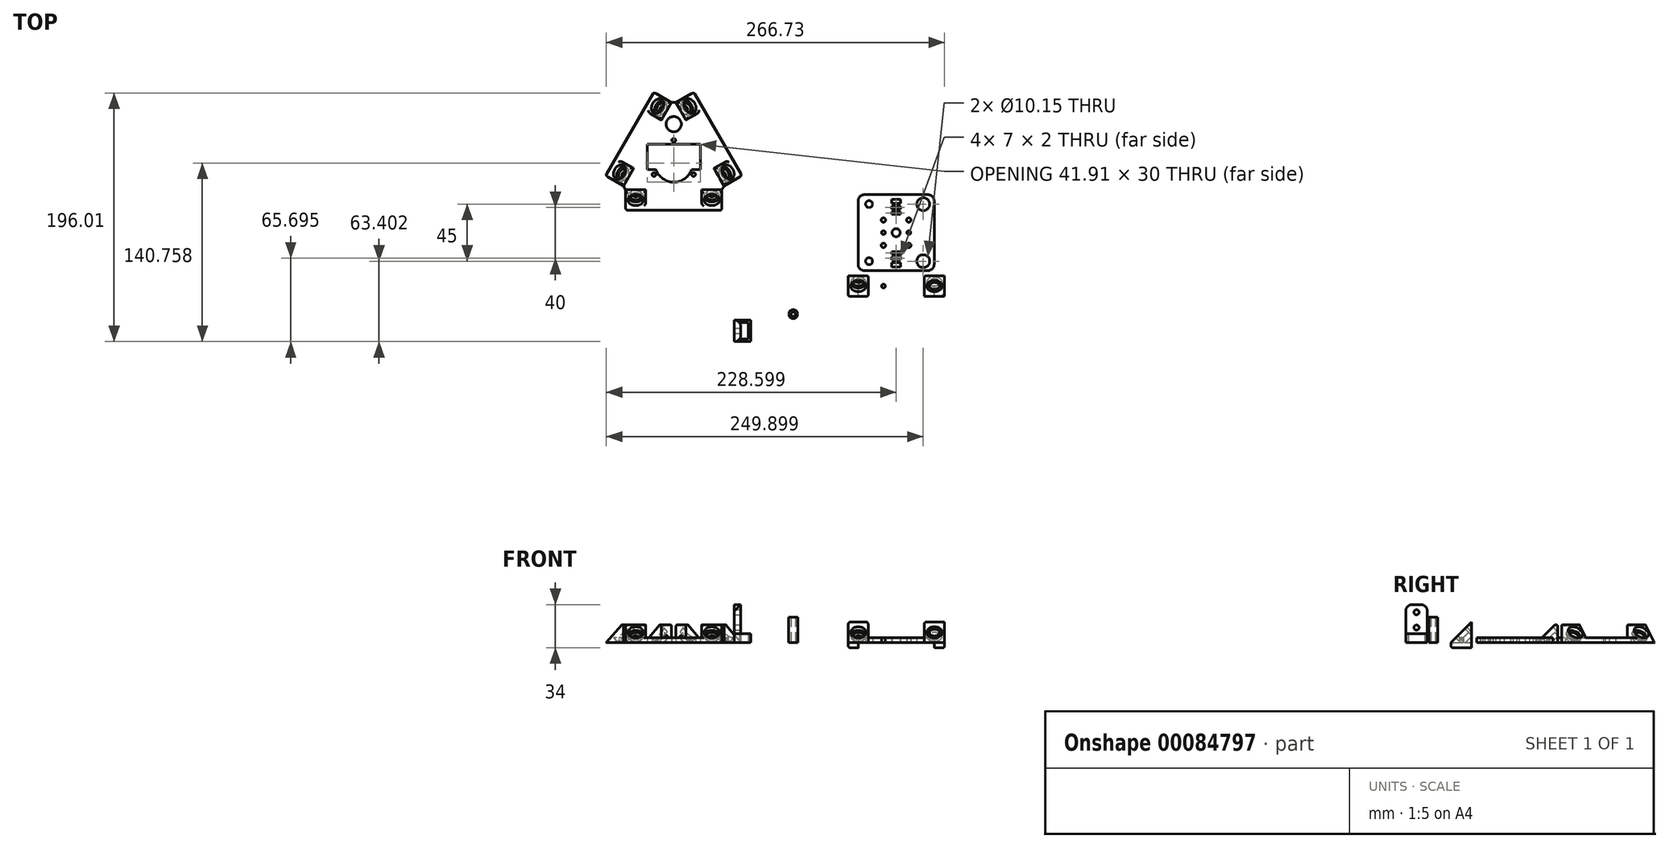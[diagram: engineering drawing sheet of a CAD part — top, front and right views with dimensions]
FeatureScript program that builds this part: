
annotation { "Feature Type Name" : "Feature", "Feature Type Description" : "" }
export const myFeature = defineFeature(function(context is Context, id is Id, definition is map)
    precondition{}
    {
        {
            var Q0;
            Q0=qCreatedBy(makeId("Top.planeOp"),FACE);
            var sketch = newSketch(context, id + "F0", { "sketchPlane" : qUnion([Q0])});
            skArc(sketch, "E0", {"start": v(24.79, -19.87) * mm, "mid": v(28.33, -18.4) * mm, "end": v(29.79, -14.87) * mm});
            skLineSegment(sketch, "E1", {"start": v(24.79, -19.87) * mm, "end": v(-25.21, -19.87) * mm});
            skArc(sketch, "E2", {"start": v(29.79, 35.13) * mm, "mid": v(28.33, 38.67) * mm, "end": v(24.79, 40.13) * mm});
            skLineSegment(sketch, "E3", {"start": v(29.79, 35.13) * mm, "end": v(29.79, -14.87) * mm});
            skArc(sketch, "E4", {"start": v(-25.21, 40.13) * mm, "mid": v(-28.75, 38.67) * mm, "end": v(-30.21, 35.13) * mm});
            skLineSegment(sketch, "E5", {"start": v(-25.21, 40.13) * mm, "end": v(24.79, 40.13) * mm});
            skArc(sketch, "E6", {"start": v(-30.21, -14.87) * mm, "mid": v(-28.75, -18.4) * mm, "end": v(-25.21, -19.87) * mm});
            skLineSegment(sketch, "E7", {"start": v(-30.21, -14.87) * mm, "end": v(-30.21, 35.13) * mm});
            skCircle(sketch, "E8", {"center": v(30, -32.16) * mm, "radius": 5.9 * mm, "construction": true});
            skCircle(sketch, "E9", {"center": v(-30, -32.16) * mm, "radius": 5.9 * mm, "construction": true});
            skLineSegment(sketch, "E10", {"start": v(-30.85, -40.13) * mm, "end": v(30.85, -40.13) * mm});
            skLineSegment(sketch, "E11", {"start": v(30.85, -23.83) * mm, "end": v(-30.85, -23.83) * mm});
            skCircle(sketch, "E12", {"center": v(21.14, 32.63) * mm, "radius": 5.08 * mm});
            skCircle(sketch, "E13", {"center": v(21.14, -12.37) * mm, "radius": 5.08 * mm});
            skCircle(sketch, "E14", {"center": v(-21.56, 32.63) * mm, "radius": 2.75 * mm});
            skCircle(sketch, "E15", {"center": v(-21.56, -12.37) * mm, "radius": 2.75 * mm});
            skCircle(sketch, "E16", {"center": v(-10.21, 20.13) * mm, "radius": 1.75 * mm});
            skCircle(sketch, "E17", {"center": v(-10.21, 0.13) * mm, "radius": 1.75 * mm});
            skCircle(sketch, "E18", {"center": v(9.79, 0.13) * mm, "radius": 1.75 * mm});
            skCircle(sketch, "E19", {"center": v(9.79, 20.13) * mm, "radius": 1.75 * mm});
            skLineSegment(sketch, "E20", {"start": v(-3.63, -6.88) * mm, "end": v(3.37, -6.88) * mm});
            skLineSegment(sketch, "E21", {"start": v(3.37, -6.88) * mm, "end": v(3.37, -4.88) * mm});
            skLineSegment(sketch, "E22", {"start": v(3.37, -4.88) * mm, "end": v(-3.63, -4.88) * mm});
            skLineSegment(sketch, "E23", {"start": v(-3.63, -4.88) * mm, "end": v(-3.63, -6.88) * mm});
            skLineSegment(sketch, "E24", {"start": v(-3.66, -11.08) * mm, "end": v(3.34, -11.08) * mm});
            skLineSegment(sketch, "E25", {"start": v(3.34, -11.08) * mm, "end": v(3.34, -9.08) * mm});
            skLineSegment(sketch, "E26", {"start": v(3.34, -9.08) * mm, "end": v(-3.66, -9.08) * mm});
            skLineSegment(sketch, "E27", {"start": v(-3.66, -9.08) * mm, "end": v(-3.66, -11.08) * mm});
            skLineSegment(sketch, "E28", {"start": v(3.35, -16.82) * mm, "end": v(3.35, -13.38) * mm});
            skLineSegment(sketch, "E29", {"start": v(3.35, -13.38) * mm, "end": v(-3.63, -13.38) * mm});
            skLineSegment(sketch, "E30", {"start": v(-3.63, 33.12) * mm, "end": v(3.37, 33.12) * mm});
            skLineSegment(sketch, "E31", {"start": v(3.37, 33.12) * mm, "end": v(3.37, 36.53) * mm});
            skLineSegment(sketch, "E32", {"start": v(3.37, 36.53) * mm, "end": v(-3.63, 36.52) * mm});
            skLineSegment(sketch, "E33", {"start": v(-3.63, 36.52) * mm, "end": v(-3.63, 33.12) * mm});
            skLineSegment(sketch, "E34", {"start": v(-3.66, 28.92) * mm, "end": v(3.34, 28.92) * mm});
            skLineSegment(sketch, "E35", {"start": v(3.34, 28.92) * mm, "end": v(3.34, 30.92) * mm});
            skLineSegment(sketch, "E36", {"start": v(3.34, 30.92) * mm, "end": v(-3.66, 30.92) * mm});
            skLineSegment(sketch, "E37", {"start": v(-3.66, 30.92) * mm, "end": v(-3.66, 28.92) * mm});
            skLineSegment(sketch, "E38", {"start": v(-3.63, 24.62) * mm, "end": v(3.37, 24.62) * mm});
            skLineSegment(sketch, "E39", {"start": v(3.37, 24.62) * mm, "end": v(3.37, 26.62) * mm});
            skLineSegment(sketch, "E40", {"start": v(3.37, 26.62) * mm, "end": v(-3.63, 26.62) * mm});
            skLineSegment(sketch, "E41", {"start": v(-3.63, 26.62) * mm, "end": v(-3.63, 24.62) * mm});
            skCircle(sketch, "E42", {"center": v(-10.21, 10.13) * mm, "radius": 1.5 * mm});
            skCircle(sketch, "E43", {"center": v(9.79, 10.13) * mm, "radius": 1.5 * mm});
            skCircle(sketch, "E44", {"center": v(-10.18, -31.98) * mm, "radius": 1.5 * mm});
            skCircle(sketch, "E45", {"center": v(9.82, -31.98) * mm, "radius": 1.5 * mm});
            skCircle(sketch, "E46", {"center": v(-0.21, 10.13) * mm, "radius": 3.2 * mm});
            skPoint(sketch, "E47", {"position": v(-3.63, 36.52) * mm});
            skLineSegment(sketch, "E48", {"start": v(-3.63, -16.82) * mm, "end": v(3.35, -16.82) * mm});
            skLineSegment(sketch, "E49", {"start": v(-3.63, -16.82) * mm, "end": v(-3.63, -13.38) * mm});
            skLineSegment(sketch, "E50.bottom", {"start": v(-30.85, -40.13) * mm, "end": v(-37.97, -40.13) * mm});
            skLineSegment(sketch, "E50.top", {"start": v(-30.85, -23.83) * mm, "end": v(-37.97, -23.83) * mm});
            skLineSegment(sketch, "E50.right", {"start": v(-37.97, -40.13) * mm, "end": v(-37.97, -23.83) * mm});
            skLineSegment(sketch, "E51", {"start": v(0, -40.13) * mm, "end": v(0, -23.83) * mm, "construction": true});
            skLineSegment(sketch, "E52.MirrorCS", {"start": v(30.85, -40.13) * mm, "end": v(37.97, -40.13) * mm});
            skLineSegment(sketch, "E53.MirrorCS", {"start": v(37.97, -40.13) * mm, "end": v(37.97, -23.83) * mm});
            skLineSegment(sketch, "E54.MirrorCS", {"start": v(30.85, -23.83) * mm, "end": v(37.97, -23.83) * mm});
            skLineSegment(sketch, "E55", {"start": v(-30, -32.16) * mm, "end": v(-30, -57.06) * mm, "construction": true});
            skLineSegment(sketch, "E56.MirrorCS", {"start": v(-22.03, -40.13) * mm, "end": v(-22.03, -23.83) * mm});
            skLineSegment(sketch, "E57", {"start": v(30, -32.16) * mm, "end": v(30, -52.4) * mm, "construction": true});
            skLineSegment(sketch, "E58.MirrorCS", {"start": v(22.03, -40.13) * mm, "end": v(22.03, -23.83) * mm});
            skLineSegment(sketch, "E59", {"start": v(-30, -40.13) * mm, "end": v(-30, -23.83) * mm});
            skLineSegment(sketch, "E60", {"start": v(30, -40.13) * mm, "end": v(30, -23.83) * mm});
            skSolve(sketch);
        }
        {
            var Q0;
            Q0=qCreatedBy(makeId("Top.planeOp"),FACE);
            var sketch = newSketch(context, id + "F1", { "sketchPlane" : qUnion([Q0])});
            skLineSegment(sketch, "E61", {"start": v(-206.4, 27.73) * mm, "end": v(-144.7, 27.73) * mm});
            skLineSegment(sketch, "E62", {"start": v(-144.7, 44.03) * mm, "end": v(-153.53, 44.03) * mm});
            skLineSegment(sketch, "E63.bottom", {"start": v(-206.4, 27.73) * mm, "end": v(-213.53, 27.73) * mm});
            skLineSegment(sketch, "E63.top", {"start": v(-206.4, 44.03) * mm, "end": v(-213.53, 44.03) * mm});
            skLineSegment(sketch, "E63.right", {"start": v(-213.53, 27.73) * mm, "end": v(-213.53, 44.03) * mm});
            skLineSegment(sketch, "E64", {"start": v(-175.56, 27.73) * mm, "end": v(-175.56, 44.03) * mm, "construction": true});
            skLineSegment(sketch, "E65.MirrorCS", {"start": v(-144.7, 27.73) * mm, "end": v(-137.59, 27.73) * mm});
            skLineSegment(sketch, "E66.MirrorCS", {"start": v(-137.59, 27.73) * mm, "end": v(-137.59, 44.03) * mm});
            skLineSegment(sketch, "E67.MirrorCS", {"start": v(-144.7, 44.03) * mm, "end": v(-137.59, 44.03) * mm});
            skLineSegment(sketch, "E68", {"start": v(-205.56, 35.7) * mm, "end": v(-205.56, 10.8) * mm, "construction": true});
            skLineSegment(sketch, "E69.MirrorCS", {"start": v(-197.59, 27.73) * mm, "end": v(-197.59, 44.03) * mm});
            skLineSegment(sketch, "E70", {"start": v(-145.56, 35.7) * mm, "end": v(-145.56, 15.46) * mm, "construction": true});
            skLineSegment(sketch, "E71.MirrorCS", {"start": v(-153.53, 27.73) * mm, "end": v(-153.53, 44.03) * mm});
            skLineSegment(sketch, "E72", {"start": v(-175.56, 44.03) * mm, "end": v(-175.56, 104.1) * mm, "construction": true});
            skLineSegment(sketch, "E73.1.0", {"start": v(-121.75, 55.16) * mm, "end": v(-135.87, 47.01) * mm});
            skLineSegment(sketch, "E73.1.1", {"start": v(-129.72, 68.97) * mm, "end": v(-143.84, 60.82) * mm});
            skLineSegment(sketch, "E73.1.2", {"start": v(-151.75, 107.12) * mm, "end": v(-165.87, 98.97) * mm});
            skLineSegment(sketch, "E73.1.3", {"start": v(-159.94, 74) * mm, "end": v(-211.96, 43.97) * mm, "construction": true});
            skLineSegment(sketch, "E73.1.4", {"start": v(-145.82, 82.15) * mm, "end": v(-159.94, 74) * mm, "construction": true});
            skLineSegment(sketch, "E73.1.5", {"start": v(-159.72, 120.93) * mm, "end": v(-173.84, 112.78) * mm});
            skLineSegment(sketch, "E73.1.6", {"start": v(-125.3, 61.33) * mm, "end": v(-156.16, 114.76) * mm});
            skLineSegment(sketch, "E73.1.7", {"start": v(-162.64, 110.04) * mm, "end": v(-145.1, 120.16) * mm, "construction": true});
            skLineSegment(sketch, "E73.1.8", {"start": v(-132.64, 58.08) * mm, "end": v(-111.08, 70.53) * mm, "construction": true});
            skLineSegment(sketch, "E73.1.9", {"start": v(-170.28, 106.61) * mm, "end": v(-165.87, 98.97) * mm});
            skLineSegment(sketch, "E73.1.12", {"start": v(-139.43, 53.18) * mm, "end": v(-135.87, 47.01) * mm});
            skLineSegment(sketch, "E73.1.13", {"start": v(-156.16, 114.76) * mm, "end": v(-159.72, 120.93) * mm});
            skLineSegment(sketch, "E73.1.14", {"start": v(-125.3, 61.33) * mm, "end": v(-121.75, 55.16) * mm});
            skLineSegment(sketch, "E73.1.15", {"start": v(-170.28, 106.61) * mm, "end": v(-173.84, 112.78) * mm});
            skLineSegment(sketch, "E73.2.0", {"start": v(-191.4, 120.93) * mm, "end": v(-177.28, 112.78) * mm});
            skLineSegment(sketch, "E73.2.1", {"start": v(-199.36, 107.12) * mm, "end": v(-185.25, 98.97) * mm});
            skLineSegment(sketch, "E73.2.2", {"start": v(-221.4, 68.97) * mm, "end": v(-207.28, 60.82) * mm});
            skLineSegment(sketch, "E73.2.3", {"start": v(-210.14, 84.95) * mm, "end": v(-144, 46.77) * mm, "construction": true});
            skLineSegment(sketch, "E73.2.4", {"start": v(-210.14, 84.95) * mm, "end": v(-210.14, 84.95) * mm});
            skLineSegment(sketch, "E73.2.5", {"start": v(-229.36, 55.16) * mm, "end": v(-215.25, 47.01) * mm});
            skLineSegment(sketch, "E73.2.6", {"start": v(-194.95, 114.76) * mm, "end": v(-225.8, 61.33) * mm});
            skLineSegment(sketch, "E73.2.7", {"start": v(-218.47, 58.08) * mm, "end": v(-236, 68.2) * mm, "construction": true});
            skLineSegment(sketch, "E73.2.8", {"start": v(-188.47, 110.04) * mm, "end": v(-210.04, 122.49) * mm, "construction": true});
            skLineSegment(sketch, "E73.2.9", {"start": v(-211.69, 53.18) * mm, "end": v(-207.28, 60.82) * mm});
            skLineSegment(sketch, "E73.2.12", {"start": v(-180.84, 106.61) * mm, "end": v(-177.28, 112.78) * mm});
            skLineSegment(sketch, "E73.2.13", {"start": v(-225.8, 61.33) * mm, "end": v(-229.36, 55.16) * mm});
            skLineSegment(sketch, "E73.2.14", {"start": v(-194.95, 114.76) * mm, "end": v(-191.4, 120.93) * mm});
            skLineSegment(sketch, "E73.2.15", {"start": v(-211.69, 53.18) * mm, "end": v(-215.25, 47.01) * mm});
            skPoint(sketch, "E73.center", {"position": v(-175.56, 64.99) * mm});
            skLineSegment(sketch, "E74", {"start": v(-215.25, 47.01) * mm, "end": v(-213.53, 44.03) * mm});
            skLineSegment(sketch, "E75", {"start": v(-135.87, 47.01) * mm, "end": v(-137.59, 44.03) * mm});
            skLineSegment(sketch, "E76", {"start": v(-177.28, 112.78) * mm, "end": v(-173.84, 112.78) * mm});
            skCircle(sketch, "E77", {"center": v(-175.56, 64.99) * mm, "radius": 15 * mm});
            skLineSegment(sketch, "E78.trimOffspring", {"start": v(-185.25, 98.97) * mm, "end": v(-180.84, 106.61) * mm});
            skLineSegment(sketch, "E79.trimOffspring", {"start": v(-143.84, 60.82) * mm, "end": v(-139.43, 53.18) * mm});
            skLineSegment(sketch, "E80.trimOffspring", {"start": v(-197.59, 44.03) * mm, "end": v(-206.4, 44.03) * mm});
            skCircle(sketch, "E81", {"center": v(-175.56, 95.72) * mm, "radius": 6 * mm});
            skCircle(sketch, "E82.cCircle", {"center": v(-175.56, 64.99) * mm, "radius": 9 * mm, "construction": true});
            skLineSegment(sketch, "E82.0", {"start": v(-159.97, 55.99) * mm, "end": v(-191.14, 55.99) * mm, "construction": true});
            skLineSegment(sketch, "E82.1", {"start": v(-191.14, 55.99) * mm, "end": v(-175.56, 82.99) * mm, "construction": true});
            skLineSegment(sketch, "E82.2", {"start": v(-175.56, 82.99) * mm, "end": v(-159.97, 55.99) * mm, "construction": true});
            skPoint(sketch, "E82.0.midPoint", {"position": v(-175.56, 55.99) * mm});
            skCircle(sketch, "E83", {"center": v(-191.14, 55.99) * mm, "radius": 1.5 * mm});
            skCircle(sketch, "E84", {"center": v(-175.56, 82.99) * mm, "radius": 1.5 * mm});
            skCircle(sketch, "E85", {"center": v(-159.97, 55.99) * mm, "radius": 1.5 * mm});
            skPoint(sketch, "E86", {"position": v(-158.23, 54.99) * mm});
            skPoint(sketch, "E87", {"position": v(-175.56, 44.99) * mm});
            skCircle(sketch, "E88.cCircle", {"center": v(-175.56, 64.99) * mm, "radius": 20 * mm, "construction": true});
            skLineSegment(sketch, "E88.0", {"start": v(-148.23, 72.3) * mm, "end": v(-168.23, 37.67) * mm, "construction": true});
            skLineSegment(sketch, "E88.1", {"start": v(-168.23, 37.67) * mm, "end": v(-202.88, 57.67) * mm, "construction": true});
            skLineSegment(sketch, "E88.2", {"start": v(-202.88, 57.67) * mm, "end": v(-182.88, 92.3) * mm, "construction": true});
            skLineSegment(sketch, "E88.3", {"start": v(-182.88, 92.3) * mm, "end": v(-148.23, 72.3) * mm, "construction": true});
            skCircle(sketch, "E89.cCircle", {"center": v(-175.56, 64.99) * mm, "radius": 20.96 * mm, "construction": true});
            skLineSegment(sketch, "E89.0", {"start": v(-154.6, 44.03) * mm, "end": v(-196.51, 44.03) * mm, "construction": true});
            skLineSegment(sketch, "E89.1", {"start": v(-196.51, 44.03) * mm, "end": v(-196.51, 85.94) * mm, "construction": true});
            skLineSegment(sketch, "E89.2", {"start": v(-196.51, 85.94) * mm, "end": v(-154.6, 85.94) * mm, "construction": true});
            skLineSegment(sketch, "E89.3", {"start": v(-154.6, 85.94) * mm, "end": v(-154.6, 44.03) * mm, "construction": true});
            skPoint(sketch, "E89.0.midPoint", {"position": v(-175.56, 44.03) * mm});
            skPoint(sketch, "E90", {"position": v(-175.56, 79.99) * mm});
            skLineSegment(sketch, "E91", {"start": v(-196.51, 79.99) * mm, "end": v(-154.6, 79.99) * mm});
            skLineSegment(sketch, "E92", {"start": v(-154.6, 79.99) * mm, "end": v(-154.6, 59.99) * mm});
            skLineSegment(sketch, "E93", {"start": v(-154.6, 59.99) * mm, "end": v(-196.51, 59.99) * mm});
            skLineSegment(sketch, "E94", {"start": v(-196.51, 59.99) * mm, "end": v(-196.51, 79.99) * mm});
            skSolve(sketch);
        }
        {
            var Q0;
            Q0=makeQuery(id+"F0.imprint","IMPRINT",FACE,{"disambiguationData":[TD([[makeQuery(id+"F0.imprint","IMPRINT",EDGE,{"derivedFrom":sQuery(id+"F0.wireOp",EDGE,"E0")}),1.0]])]});
            var Q1;
            Q1=makeQuery(id+"F0.imprint","IMPRINT",FACE,{"disambiguationData":[TD([[makeQuery(id+"F0.imprint","IMPRINT",EDGE,{"derivedFrom":sQuery(id+"F0.wireOp",EDGE,"f96d0108-ce3c-40f9-9041-a5f02a56c2c8")}),-1.0]])]});
            var Q2;
            Q2=makeQuery(id+"F0.imprint","IMPRINT",FACE,{"disambiguationData":[TD([[makeQuery(id+"F0.imprint","IMPRINT",EDGE,{"derivedFrom":sQuery(id+"F0.wireOp",EDGE,"fc6a74a1-8ae2-464b-8a54-e97a179053b1")}),1.0]])]});
            var Q3;
            Q3=makeQuery(id+"F0.imprint","IMPRINT",FACE,{"disambiguationData":[TD([[makeQuery(id+"F0.imprint","IMPRINT",EDGE,{"derivedFrom":sQuery(id+"F0.wireOp",EDGE,"d8805900-849d-46b7-a423-43423c13d2e1")}),-1.0]])]});
            var Q4;
            Q4=makeQuery(id+"F0.imprint","IMPRINT",FACE,{"disambiguationData":[TD([[makeQuery(id+"F0.imprint","IMPRINT",EDGE,{"derivedFrom":sQuery(id+"F0.wireOp",EDGE,"6a2c02a0-f174-49b4-8e9f-637eccd819cc")}),-1.0]])]});
            var Q5;
            Q5=makeQuery(id+"F0.imprint","IMPRINT",FACE,{"disambiguationData":[TD([[makeQuery(id+"F0.imprint","IMPRINT",EDGE,{"derivedFrom":sQuery(id+"F0.wireOp",EDGE,"E44")}),1.0]])]});
            var Q6;
            {var subQ1=sQuery(id+"F1.wireOp",EDGE,"E73.2.1");Q6=makeQuery(id+"F1.imprint","IMPRINT",FACE,{"disambiguationData":[TD([[makeQuery(id+"F1.imprint","IMPRINT",EDGE,{"derivedFrom":subQ1}),-1.0]])]});}
            var Q7;
            {var subQ12=sQuery(id+"F1.wireOp",EDGE,"E63.top");Q7=makeQuery(id+"F1.imprint","IMPRINT",FACE,{"disambiguationData":[TD([[makeQuery(id+"F1.imprint","IMPRINT",EDGE,{"derivedFrom":subQ12}),-1.0]])]});}
            var Q8;
            {var subQ1=sQuery(id+"F1.wireOp",EDGE,"E73.1.1");Q8=makeQuery(id+"F1.imprint","IMPRINT",FACE,{"disambiguationData":[TD([[makeQuery(id+"F1.imprint","IMPRINT",EDGE,{"derivedFrom":subQ1}),-1.0]])]});}
            var Q9;
            Q9=makeQuery(id+"F1.imprint","IMPRINT",FACE,{"disambiguationData":[TD([[makeQuery(id+"F1.imprint","IMPRINT",EDGE,{"derivedFrom":sQuery(id+"F1.wireOp",EDGE,"f1ae98ec-eddd-4e72-9429-8ecdf1ed458a")}),1.0]])]});
            var Q10;
            Q10=makeQuery(id+"F1.imprint","IMPRINT",FACE,{"disambiguationData":[TD([[makeQuery(id+"F1.imprint","IMPRINT",EDGE,{"derivedFrom":sQuery(id+"F1.wireOp",EDGE,"E66.MirrorCS")}),-1.0]])]});
            var Q11;
            Q11=makeQuery(id+"F1.imprint","IMPRINT",FACE,{"disambiguationData":[TD([[makeQuery(id+"F1.imprint","IMPRINT",EDGE,{"derivedFrom":sQuery(id+"F1.wireOp",EDGE,"E63.right")}),1.0]])]});
            var Q12;
            Q12=makeQuery(id+"F1.imprint","IMPRINT",FACE,{"disambiguationData":[TD([[makeQuery(id+"F1.imprint","IMPRINT",EDGE,{"derivedFrom":sQuery(id+"F1.wireOp",EDGE,"E73.1.5")}),-1.0]])]});
            extrude(context, id + "F2", {"entities" : qUnion([Q0, Q1, Q2, Q3, Q4, Q5, Q6, Q7, Q8, Q9, Q10, Q11, Q12]), "depth" : 4 * mm});
        }
        {
            var Q0;
            Q0=makeQuery(id+"F0.imprint","IMPRINT",FACE,{"disambiguationData":[TD([[makeQuery(id+"F0.imprint","IMPRINT",EDGE,{"derivedFrom":sQuery(id+"F0.wireOp",EDGE,"E9")}),-1.0]])]});
            var Q1;
            Q1=makeQuery(id+"F0.imprint","IMPRINT",FACE,{"disambiguationData":[TD([[makeQuery(id+"F0.imprint","IMPRINT",EDGE,{"derivedFrom":sQuery(id+"F0.wireOp",EDGE,"E8")}),1.0]])]});
            var Q2;
            Q2=makeQuery(id+"F0.imprint","IMPRINT",FACE,{"disambiguationData":[TD([[makeQuery(id+"F0.imprint","IMPRINT",EDGE,{"derivedFrom":sQuery(id+"F0.wireOp",EDGE,"E8")}),-1.0]])]});
            var Q3;
            Q3=makeQuery(id+"F0.imprint","IMPRINT",FACE,{"disambiguationData":[TD([[makeQuery(id+"F0.imprint","IMPRINT",EDGE,{"derivedFrom":sQuery(id+"F0.wireOp",EDGE,"E9")}),1.0]])]});
            var Q4;
            Q4=makeQuery(id+"F1.imprint","IMPRINT",FACE,{"disambiguationData":[TD([[makeQuery(id+"F1.imprint","IMPRINT",EDGE,{"derivedFrom":sQuery(id+"F1.wireOp",EDGE,"346c870d-bf97-44aa-bfb7-157ee8bb922b.2.6")}),1.0]])]});
            var Q5;
            Q5=makeQuery(id+"F1.imprint","IMPRINT",FACE,{"disambiguationData":[TD([[makeQuery(id+"F1.imprint","IMPRINT",EDGE,{"derivedFrom":sQuery(id+"F1.wireOp",EDGE,"346c870d-bf97-44aa-bfb7-157ee8bb922b.2.5")}),1.0]])]});
            var Q6;
            Q6=makeQuery(id+"F1.imprint","IMPRINT",FACE,{"disambiguationData":[TD([[makeQuery(id+"F1.imprint","IMPRINT",EDGE,{"derivedFrom":sQuery(id+"F1.wireOp",EDGE,"346c870d-bf97-44aa-bfb7-157ee8bb922b.2.5")}),-1.0]])]});
            var Q7;
            Q7=makeQuery(id+"F1.imprint","IMPRINT",FACE,{"disambiguationData":[TD([[makeQuery(id+"F1.imprint","IMPRINT",EDGE,{"derivedFrom":sQuery(id+"F1.wireOp",EDGE,"346c870d-bf97-44aa-bfb7-157ee8bb922b.2.6")}),-1.0]])]});
            var Q8;
            Q8=makeQuery(id+"F1.imprint","IMPRINT",FACE,{"disambiguationData":[TD([[makeQuery(id+"F1.imprint","IMPRINT",EDGE,{"derivedFrom":sQuery(id+"F1.wireOp",EDGE,"1521ab2a-ef47-4488-a64c-4af944e9871a")}),-1.0]])]});
            var Q9;
            Q9=makeQuery(id+"F1.imprint","IMPRINT",FACE,{"disambiguationData":[TD([[makeQuery(id+"F1.imprint","IMPRINT",EDGE,{"derivedFrom":sQuery(id+"F1.wireOp",EDGE,"1521ab2a-ef47-4488-a64c-4af944e9871a")}),1.0]])]});
            var Q10;
            Q10=makeQuery(id+"F1.imprint","IMPRINT",FACE,{"disambiguationData":[TD([[makeQuery(id+"F1.imprint","IMPRINT",EDGE,{"derivedFrom":sQuery(id+"F1.wireOp",EDGE,"f8b58d7a-966b-4f00-93db-83ad977ebcb6")}),1.0]])]});
            var Q11;
            Q11=makeQuery(id+"F1.imprint","IMPRINT",FACE,{"disambiguationData":[TD([[makeQuery(id+"F1.imprint","IMPRINT",EDGE,{"derivedFrom":sQuery(id+"F1.wireOp",EDGE,"f8b58d7a-966b-4f00-93db-83ad977ebcb6")}),-1.0]])]});
            var Q12;
            Q12=makeQuery(id+"F1.imprint","IMPRINT",FACE,{"disambiguationData":[TD([[makeQuery(id+"F1.imprint","IMPRINT",EDGE,{"derivedFrom":sQuery(id+"F1.wireOp",EDGE,"346c870d-bf97-44aa-bfb7-157ee8bb922b.1.5")}),1.0]])]});
            var Q13;
            Q13=makeQuery(id+"F1.imprint","IMPRINT",FACE,{"disambiguationData":[TD([[makeQuery(id+"F1.imprint","IMPRINT",EDGE,{"derivedFrom":sQuery(id+"F1.wireOp",EDGE,"346c870d-bf97-44aa-bfb7-157ee8bb922b.1.5")}),-1.0]])]});
            var Q14;
            Q14=makeQuery(id+"F1.imprint","IMPRINT",FACE,{"disambiguationData":[TD([[makeQuery(id+"F1.imprint","IMPRINT",EDGE,{"derivedFrom":sQuery(id+"F1.wireOp",EDGE,"346c870d-bf97-44aa-bfb7-157ee8bb922b.1.6")}),1.0]])]});
            var Q15;
            Q15=makeQuery(id+"F1.imprint","IMPRINT",FACE,{"disambiguationData":[TD([[makeQuery(id+"F1.imprint","IMPRINT",EDGE,{"derivedFrom":sQuery(id+"F1.wireOp",EDGE,"346c870d-bf97-44aa-bfb7-157ee8bb922b.1.6")}),-1.0]])]});
            var Q16;
            {var subQ1=sQuery(id+"F1.wireOp",EDGE,"E63.bottom");Q16=makeQuery(id+"F1.imprint","IMPRINT",FACE,{"disambiguationData":[TD([[makeQuery(id+"F1.imprint","IMPRINT",EDGE,{"derivedFrom":subQ1}),-1.0]])]});}
            var Q17;
            {var subQ1=sQuery(id+"F1.wireOp",EDGE,"E73.2.2");Q17=makeQuery(id+"F1.imprint","IMPRINT",FACE,{"disambiguationData":[TD([[makeQuery(id+"F1.imprint","IMPRINT",EDGE,{"derivedFrom":subQ1}),-1.0]])]});}
            var Q18;
            Q18=makeQuery(id+"F1.imprint","IMPRINT",FACE,{"disambiguationData":[TD([[makeQuery(id+"F1.imprint","IMPRINT",EDGE,{"derivedFrom":sQuery(id+"F1.wireOp",EDGE,"E73.2.0")}),-1.0]])]});
            var Q19;
            {var subQ1=sQuery(id+"F1.wireOp",EDGE,"E73.1.2");Q19=makeQuery(id+"F1.imprint","IMPRINT",FACE,{"disambiguationData":[TD([[makeQuery(id+"F1.imprint","IMPRINT",EDGE,{"derivedFrom":subQ1}),-1.0]])]});}
            var Q20;
            Q20=makeQuery(id+"F1.imprint","IMPRINT",FACE,{"disambiguationData":[TD([[makeQuery(id+"F1.imprint","IMPRINT",EDGE,{"derivedFrom":sQuery(id+"F1.wireOp",EDGE,"E73.1.0")}),-1.0]])]});
            var Q21;
            {var subQ0=sQuery(id+"F1.wireOp",EDGE,"E65.MirrorCS");Q21=makeQuery(id+"F1.imprint","IMPRINT",FACE,{"disambiguationData":[TD([[makeQuery(id+"F1.imprint","IMPRINT",EDGE,{"derivedFrom":subQ0}),1.0]])]});}
            var Q22;
            {var subQ0=sQuery(id+"F0.wireOp",EDGE,"E56.MirrorCS");Q22=makeQuery(id+"F0.imprint","IMPRINT",FACE,{"disambiguationData":[TD([[makeQuery(id+"F0.imprint","IMPRINT",EDGE,{"derivedFrom":subQ0}),1.0]])]});}
            var Q23;
            {var subQ1=sQuery(id+"F0.wireOp",EDGE,"E50.bottom");Q23=makeQuery(id+"F0.imprint","IMPRINT",FACE,{"disambiguationData":[TD([[makeQuery(id+"F0.imprint","IMPRINT",EDGE,{"derivedFrom":subQ1}),-1.0]])]});}
            var Q24;
            {var subQ0=sQuery(id+"F0.wireOp",EDGE,"E58.MirrorCS");Q24=makeQuery(id+"F0.imprint","IMPRINT",FACE,{"disambiguationData":[TD([[makeQuery(id+"F0.imprint","IMPRINT",EDGE,{"derivedFrom":subQ0}),-1.0]])]});}
            var Q25;
            {var subQ0=sQuery(id+"F0.wireOp",EDGE,"E52.MirrorCS");Q25=makeQuery(id+"F0.imprint","IMPRINT",FACE,{"disambiguationData":[TD([[makeQuery(id+"F0.imprint","IMPRINT",EDGE,{"derivedFrom":subQ0}),1.0]])]});}
            extrude(context, id + "F3", {"entities" : qUnion([Q0, Q1, Q2, Q3, Q4, Q5, Q6, Q7, Q8, Q9, Q10, Q11, Q12, Q13, Q14, Q15, Q16, Q17, Q18, Q19, Q20, Q21, Q22, Q23, Q24, Q25]), "operationType" : NewBodyOperationType.ADD, "depth" : 16.3 * mm});
        }
        {
            var Q0;
            {var subQ0=sQuery(id+"F0.wireOp",EDGE,"E52.MirrorCS");Q0=makeQuery(id+"F0.imprint","IMPRINT",FACE,{"disambiguationData":[TD([[makeQuery(id+"F0.imprint","IMPRINT",EDGE,{"derivedFrom":subQ0}),1.0]])]});}
            var Q1;
            {var subQ1=sQuery(id+"F0.wireOp",EDGE,"E50.bottom");Q1=makeQuery(id+"F0.imprint","IMPRINT",FACE,{"disambiguationData":[TD([[makeQuery(id+"F0.imprint","IMPRINT",EDGE,{"derivedFrom":subQ1}),-1.0]])]});}
            extrude(context, id + "F4", {"entities" : qUnion([Q0, Q1]), "operationType" : NewBodyOperationType.ADD, "oppositeDirection" : true, "depth" : 4 * mm});
        }
        {
            var Q0;
            Q0=makeQuery(id+"F3.opExtrude","CAP_EDGE",EDGE,{"disambiguationData":[OSD([sQuery(id+"F0.wireOp",EDGE,"E10"),sQuery(id+"F0.wireOp",EDGE,"E50.bottom")])],"isStart":false});
            var Q1;
            Q1=makeQuery(id+"F3.opExtrude","CAP_EDGE",EDGE,{"disambiguationData":[OSD([sQuery(id+"F0.wireOp",EDGE,"E10"),sQuery(id+"F0.wireOp",EDGE,"E52.MirrorCS")])],"isStart":false});
            var Q2;
            Q2=makeQuery(id+"F3.opExtrude","CAP_EDGE",EDGE,{"disambiguationData":[OSD([sQuery(id+"F1.wireOp",EDGE,"E73.2.6"),sQuery(id+"F1.wireOp",EDGE,"E73.2.13")])],"isStart":false});
            var Q3;
            Q3=makeQuery(id+"F3.opExtrude","CAP_EDGE",EDGE,{"disambiguationData":[OSD([sQuery(id+"F1.wireOp",EDGE,"E73.1.6"),sQuery(id+"F1.wireOp",EDGE,"E73.1.13")])],"isStart":false});
            var Q4;
            Q4=makeQuery(id+"F3.opExtrude","CAP_EDGE",EDGE,{"disambiguationData":[OSD([sQuery(id+"F1.wireOp",EDGE,"E61"),sQuery(id+"F1.wireOp",EDGE,"E65.MirrorCS")])],"isStart":false});
            chamfer(context, id + "F5", {"entities" : qUnion([Q0, Q1, Q2, Q3, Q4]), "width" : 16.3 * mm, "tangentPropagation" : true});
        }
        {
            var Q0;
            Q0=makeQuery(id+"F5.opChamfer","BLEND_FACE",FACE,{"disambiguationData":[OSD([sQuery(id+"F0.wireOp",EDGE,"E10"),sQuery(id+"F0.wireOp",EDGE,"E50.bottom")])]});
            var sketch = newSketch(context, id + "F6", { "sketchPlane" : qUnion([Q0])});
            skLineSegment(sketch, "E95", {"start": v(-22.03, -5.33) * mm, "end": v(-37.97, -28.38) * mm, "construction": true});
            skLineSegment(sketch, "E96", {"start": v(-37.97, -28.38) * mm, "end": v(22.03, -5.33) * mm, "construction": true});
            skLineSegment(sketch, "E97", {"start": v(22.03, -5.33) * mm, "end": v(37.97, -28.38) * mm, "construction": true});
            skCircle(sketch, "E98", {"center": v(30, -16.85) * mm, "radius": 6.15 * mm});
            skCircle(sketch, "E99", {"center": v(-30, -16.85) * mm, "radius": 6.15 * mm});
            skCircle(sketch, "E100", {"center": v(-30, -16.85) * mm, "radius": 4 * mm});
            skCircle(sketch, "E101", {"center": v(30, -16.85) * mm, "radius": 4 * mm});
            skSolve(sketch);
        }
        {
            var Q0;
            {var subQ10=sQuery(id+"F1.wireOp",EDGE,"E61");var subQ11=sQuery(id+"F1.wireOp",EDGE,"E66.MirrorCS");var subQ28=sQuery(id+"F1.wireOp",EDGE,"E65.MirrorCS");Q0=makeQuery(id+"FdkW4cJf3UBl0qU_7.boolean.opBoolean","SPLIT",FACE,{"disambiguationData":[TD([makeQuery(id+"F3.opExtrude","SWEPT_FACE",FACE,{"disambiguationData":[OSD([subQ11])]})])],"derivedFrom":makeQuery(id+"F5.opChamfer","BLEND_FACE",FACE,{"disambiguationData":[OSD([subQ10,subQ28])]})});}
            var sketch = newSketch(context, id + "F7", { "sketchPlane" : qUnion([Q0])});
            skLineSegment(sketch, "E102", {"start": v(-153.53, 42.66) * mm, "end": v(-137.59, 19.6) * mm, "construction": true});
            skCircle(sketch, "E103", {"center": v(-145.56, 31.14) * mm, "radius": 6.15 * mm});
            skCircle(sketch, "E104", {"center": v(-145.56, 31.14) * mm, "radius": 4 * mm});
            skSolve(sketch);
        }
        {
            var Q0;
            {var subQ10=sQuery(id+"F1.wireOp",EDGE,"E61");var subQ12=sQuery(id+"F1.wireOp",EDGE,"E63.right");var subQ28=sQuery(id+"F1.wireOp",EDGE,"E65.MirrorCS");Q0=makeQuery(id+"FdkW4cJf3UBl0qU_7.boolean.opBoolean","SPLIT",FACE,{"disambiguationData":[TD([makeQuery(id+"F3.opExtrude","SWEPT_FACE",FACE,{"disambiguationData":[OSD([subQ12])]})])],"derivedFrom":makeQuery(id+"F5.opChamfer","BLEND_FACE",FACE,{"disambiguationData":[OSD([subQ10,subQ28])]})});}
            var sketch = newSketch(context, id + "F8", { "sketchPlane" : qUnion([Q0])});
            skCircle(sketch, "E105", {"center": v(-205.56, 31.14) * mm, "radius": 6.15 * mm});
            skCircle(sketch, "E106", {"center": v(-205.56, 31.14) * mm, "radius": 4 * mm});
            skSolve(sketch);
        }
        {
            var Q0;
            Q0=makeQuery(id+"F5.opChamfer","BLEND_FACE",FACE,{"disambiguationData":[OSD([sQuery(id+"F1.wireOp",EDGE,"E73.1.6"),sQuery(id+"F1.wireOp",EDGE,"E73.1.13")])]});
            var sketch = newSketch(context, id + "F9", { "sketchPlane" : qUnion([Q0])});
            skLineSegment(sketch, "E107", {"start": v(-111.36, 49.34) * mm, "end": v(-139.3, 47.1) * mm, "construction": true});
            skLineSegment(sketch, "E108", {"start": v(-139.3, 47.1) * mm, "end": v(-167.16, 81.23) * mm, "construction": true});
            skLineSegment(sketch, "E109", {"start": v(-167.16, 81.23) * mm, "end": v(-159.39, 108.16) * mm, "construction": true});
            skCircle(sketch, "E110", {"center": v(-125.33, 48.22) * mm, "radius": 6.15 * mm});
            skCircle(sketch, "E111", {"center": v(-163.27, 94.7) * mm, "radius": 6.15 * mm});
            skCircle(sketch, "E112", {"center": v(-125.33, 48.22) * mm, "radius": 4 * mm});
            skCircle(sketch, "E113", {"center": v(-163.27, 94.7) * mm, "radius": 4 * mm});
            skSolve(sketch);
        }
        {
            var Q0;
            Q0=makeQuery(id+"F5.opChamfer","BLEND_FACE",FACE,{"disambiguationData":[OSD([sQuery(id+"F1.wireOp",EDGE,"E73.2.6"),sQuery(id+"F1.wireOp",EDGE,"E73.2.13")])]});
            var sketch = newSketch(context, id + "F10", { "sketchPlane" : qUnion([Q0])});
            skLineSegment(sketch, "E114", {"start": v(-118.2, 108.16) * mm, "end": v(-110.42, 81.23) * mm, "construction": true});
            skLineSegment(sketch, "E115", {"start": v(-110.42, 81.23) * mm, "end": v(-138.28, 47.1) * mm, "construction": true});
            skLineSegment(sketch, "E116", {"start": v(-138.28, 47.1) * mm, "end": v(-166.22, 49.34) * mm, "construction": true});
            skCircle(sketch, "E117", {"center": v(-152.25, 48.22) * mm, "radius": 6.15 * mm});
            skCircle(sketch, "E118", {"center": v(-114.3, 94.7) * mm, "radius": 6.15 * mm});
            skCircle(sketch, "E119", {"center": v(-152.25, 48.22) * mm, "radius": 4 * mm});
            skCircle(sketch, "E120", {"center": v(-114.3, 94.7) * mm, "radius": 4 * mm});
            skSolve(sketch);
        }
        {
            var Q0;
            Q0=makeQuery(id+"F7.imprint","IMPRINT",FACE,{"disambiguationData":[TD([[makeQuery(id+"F7.imprint","IMPRINT",EDGE,{"derivedFrom":sQuery(id+"F7.wireOp",EDGE,"E103")}),1.0]])]});
            var Q1;
            Q1=makeQuery(id+"F8.imprint","IMPRINT",FACE,{"disambiguationData":[TD([[makeQuery(id+"F8.imprint","IMPRINT",EDGE,{"derivedFrom":sQuery(id+"F8.wireOp",EDGE,"E105")}),1.0]])]});
            var Q2;
            Q2=makeQuery(id+"F6.imprint","IMPRINT",FACE,{"disambiguationData":[TD([[makeQuery(id+"F6.imprint","IMPRINT",EDGE,{"derivedFrom":sQuery(id+"F6.wireOp",EDGE,"E98")}),1.0]])]});
            var Q3;
            Q3=makeQuery(id+"F6.imprint","IMPRINT",FACE,{"disambiguationData":[TD([[makeQuery(id+"F6.imprint","IMPRINT",EDGE,{"derivedFrom":sQuery(id+"F6.wireOp",EDGE,"E99")}),1.0]])]});
            extrude(context, id + "F11", {"entities" : qUnion([Q0, Q1, Q2, Q3]), "operationType" : NewBodyOperationType.REMOVE, "oppositeDirection" : true, "depth" : 4 * mm});
        }
        {
            var Q0;
            {var subQ0=sQuery(id+"F0.wireOp",EDGE,"E11");Q0=makeQuery(id+"F5.opChamfer","BLEND_EDGE",EDGE,{"disambiguationData":[OD(0.0)],"blendedFrom":[makeQuery(id+"F3.opExtrude","CAP_EDGE",EDGE,{"disambiguationData":[OSD([sQuery(id+"F0.wireOp",EDGE,"E10"),sQuery(id+"F0.wireOp",EDGE,"E50.bottom")])],"isStart":false}),makeQuery(id+"F3.boolean.opBoolean","MERGE",FACE,{"derivedFrom":[makeQuery(id+"F2.opExtrude","SWEPT_FACE",FACE,{"disambiguationData":[OSD([subQ0])]}),makeQuery(id+"F3.opExtrude","SWEPT_FACE",FACE,{"disambiguationData":[OSD([subQ0,sQuery(id+"F0.wireOp",EDGE,"E54.MirrorCS")])]}),makeQuery(id+"F3.opExtrude","SWEPT_FACE",FACE,{"disambiguationData":[OSD([subQ0,sQuery(id+"F0.wireOp",EDGE,"E50.top")])]})]})],"blendedInto":[makeQuery(id+"F3.boolean.opBoolean","MERGE",FACE,{"derivedFrom":[makeQuery(id+"F2.opExtrude","SWEPT_FACE",FACE,{"disambiguationData":[OSD([subQ0])]}),makeQuery(id+"F3.opExtrude","SWEPT_FACE",FACE,{"disambiguationData":[OSD([subQ0,sQuery(id+"F0.wireOp",EDGE,"E54.MirrorCS")])]}),makeQuery(id+"F3.opExtrude","SWEPT_FACE",FACE,{"disambiguationData":[OSD([subQ0,sQuery(id+"F0.wireOp",EDGE,"E50.top")])]})]})]});}
            var Q1;
            {var subQ0=sQuery(id+"F0.wireOp",EDGE,"E11");Q1=makeQuery(id+"F5.opChamfer","BLEND_EDGE",EDGE,{"disambiguationData":[OD(1.0)],"blendedFrom":[makeQuery(id+"F3.opExtrude","CAP_EDGE",EDGE,{"disambiguationData":[OSD([sQuery(id+"F0.wireOp",EDGE,"E10"),sQuery(id+"F0.wireOp",EDGE,"E50.bottom")])],"isStart":false}),makeQuery(id+"F3.boolean.opBoolean","MERGE",FACE,{"derivedFrom":[makeQuery(id+"F2.opExtrude","SWEPT_FACE",FACE,{"disambiguationData":[OSD([subQ0])]}),makeQuery(id+"F3.opExtrude","SWEPT_FACE",FACE,{"disambiguationData":[OSD([subQ0,sQuery(id+"F0.wireOp",EDGE,"E54.MirrorCS")])]}),makeQuery(id+"F3.opExtrude","SWEPT_FACE",FACE,{"disambiguationData":[OSD([subQ0,sQuery(id+"F0.wireOp",EDGE,"E50.top")])]})]})],"blendedInto":[makeQuery(id+"F3.boolean.opBoolean","MERGE",FACE,{"derivedFrom":[makeQuery(id+"F2.opExtrude","SWEPT_FACE",FACE,{"disambiguationData":[OSD([subQ0])]}),makeQuery(id+"F3.opExtrude","SWEPT_FACE",FACE,{"disambiguationData":[OSD([subQ0,sQuery(id+"F0.wireOp",EDGE,"E54.MirrorCS")])]}),makeQuery(id+"F3.opExtrude","SWEPT_FACE",FACE,{"disambiguationData":[OSD([subQ0,sQuery(id+"F0.wireOp",EDGE,"E50.top")])]})]})]});}
            var Q2;
            Q2=makeQuery(id+"F5.opChamfer","BLEND_EDGE",EDGE,{"blendedFrom":[makeQuery(id+"F3.opExtrude","CAP_EDGE",EDGE,{"disambiguationData":[OSD([sQuery(id+"F0.wireOp",EDGE,"E10"),sQuery(id+"F0.wireOp",EDGE,"E50.bottom")])],"isStart":false}),makeQuery(id+"F3.opExtrude","SWEPT_FACE",FACE,{"disambiguationData":[OSD([sQuery(id+"F0.wireOp",EDGE,"E53.MirrorCS")])]})],"blendedInto":[makeQuery(id+"F3.opExtrude","SWEPT_FACE",FACE,{"disambiguationData":[OSD([sQuery(id+"F0.wireOp",EDGE,"E53.MirrorCS")])]})]});
            var Q3;
            Q3=makeQuery(id+"F5.opChamfer","BLEND_EDGE",EDGE,{"blendedFrom":[makeQuery(id+"F3.opExtrude","CAP_EDGE",EDGE,{"disambiguationData":[OSD([sQuery(id+"F0.wireOp",EDGE,"E10"),sQuery(id+"F0.wireOp",EDGE,"E50.bottom")])],"isStart":false}),makeQuery(id+"F3.opExtrude","SWEPT_FACE",FACE,{"disambiguationData":[OSD([sQuery(id+"F0.wireOp",EDGE,"E58.MirrorCS")])]})],"blendedInto":[makeQuery(id+"F3.opExtrude","SWEPT_FACE",FACE,{"disambiguationData":[OSD([sQuery(id+"F0.wireOp",EDGE,"E58.MirrorCS")])]})]});
            var Q4;
            Q4=makeQuery(id+"F5.opChamfer","BLEND_EDGE",EDGE,{"blendedFrom":[makeQuery(id+"F3.opExtrude","CAP_EDGE",EDGE,{"disambiguationData":[OSD([sQuery(id+"F0.wireOp",EDGE,"E10"),sQuery(id+"F0.wireOp",EDGE,"E50.bottom")])],"isStart":false}),makeQuery(id+"F3.opExtrude","SWEPT_FACE",FACE,{"disambiguationData":[OSD([sQuery(id+"F0.wireOp",EDGE,"E56.MirrorCS")])]})],"blendedInto":[makeQuery(id+"F3.opExtrude","SWEPT_FACE",FACE,{"disambiguationData":[OSD([sQuery(id+"F0.wireOp",EDGE,"E56.MirrorCS")])]})]});
            var Q5;
            Q5=makeQuery(id+"F2.opExtrude","CAP_EDGE",EDGE,{"disambiguationData":[OSD([sQuery(id+"F0.wireOp",EDGE,"E56.MirrorCS")])],"isStart":false});
            var Q6;
            Q6=makeQuery(id+"F3.opExtrude","SWEPT_EDGE",EDGE,{"disambiguationData":[OSD([sQuery(id+"F0.wireOp",EDGE,"E11"),sQuery(id+"F0.wireOp",EDGE,"E56.MirrorCS")])]});
            var Q7;
            Q7=makeQuery(id+"F3.opExtrude","SWEPT_EDGE",EDGE,{"disambiguationData":[OSD([sQuery(id+"F0.wireOp",EDGE,"E11"),sQuery(id+"F0.wireOp",EDGE,"E58.MirrorCS")])]});
            var Q8;
            Q8=makeQuery(id+"F5.opChamfer","BLEND_EDGE",EDGE,{"blendedFrom":[makeQuery(id+"F3.opExtrude","CAP_EDGE",EDGE,{"disambiguationData":[OSD([sQuery(id+"F0.wireOp",EDGE,"E10"),sQuery(id+"F0.wireOp",EDGE,"E50.bottom")])],"isStart":false}),makeQuery(id+"F3.opExtrude","SWEPT_FACE",FACE,{"disambiguationData":[OSD([sQuery(id+"F0.wireOp",EDGE,"E50.right")])]})],"blendedInto":[makeQuery(id+"F3.opExtrude","SWEPT_FACE",FACE,{"disambiguationData":[OSD([sQuery(id+"F0.wireOp",EDGE,"E50.right")])]})]});
            var Q9;
            Q9=makeQuery(id+"F2.opExtrude","CAP_EDGE",EDGE,{"disambiguationData":[OSD([sQuery(id+"F0.wireOp",EDGE,"E58.MirrorCS")])],"isStart":false});
            var Q10;
            {var subQ0=sQuery(id+"F0.wireOp",EDGE,"E50.right");var subQ1=sQuery(id+"F0.wireOp",EDGE,"E50.bottom");Q10=makeQuery(id+"F4.boolean.opBoolean","MERGE",EDGE,{"derivedFrom":[makeQuery(id+"F3.opExtrude","SWEPT_EDGE",EDGE,{"disambiguationData":[OSD([subQ1,subQ0])]}),makeQuery(id+"F4.opExtrude","SWEPT_EDGE",EDGE,{"disambiguationData":[OSD([subQ1,subQ0])]})]});}
            var Q11;
            Q11=makeQuery(id+"F4.opExtrude","CAP_EDGE",EDGE,{"disambiguationData":[OSD([sQuery(id+"F0.wireOp",EDGE,"E10"),sQuery(id+"F0.wireOp",EDGE,"E52.MirrorCS")])],"isStart":false});
            var Q12;
            Q12=makeQuery(id+"F4.opExtrude","CAP_EDGE",EDGE,{"disambiguationData":[OSD([sQuery(id+"F0.wireOp",EDGE,"E53.MirrorCS")])],"isStart":false});
            var Q13;
            Q13=makeQuery(id+"F4.opExtrude","CAP_EDGE",EDGE,{"disambiguationData":[OSD([sQuery(id+"F0.wireOp",EDGE,"E50.right")])],"isStart":false});
            var Q14;
            Q14=makeQuery(id+"F4.opExtrude","CAP_EDGE",EDGE,{"disambiguationData":[OSD([sQuery(id+"F0.wireOp",EDGE,"E10"),sQuery(id+"F0.wireOp",EDGE,"E50.bottom")])],"isStart":false});
            fillet(context, id + "F12", {"entities" : qUnion([Q0, Q1, Q2, Q3, Q4, Q5, Q6, Q7, Q8, Q9, Q10, Q11, Q12, Q13, Q14]), "radius" : 1.5 * mm, "tangentPropagation" : true, "allowEdgeOverflow" : false});
        }
        {
            var Q0;
            Q0=makeQuery(id+"F5.opChamfer","BLEND_EDGE",EDGE,{"blendedFrom":[makeQuery(id+"F3.opExtrude","CAP_EDGE",EDGE,{"disambiguationData":[OSD([sQuery(id+"F1.wireOp",EDGE,"E73.2.6"),sQuery(id+"F1.wireOp",EDGE,"E73.2.13")])],"isStart":false}),makeQuery(id+"F3.opExtrude","SWEPT_FACE",FACE,{"disambiguationData":[OSD([sQuery(id+"F1.wireOp",EDGE,"E73.2.9"),sQuery(id+"F1.wireOp",EDGE,"E73.2.15")])]})],"blendedInto":[makeQuery(id+"F3.opExtrude","SWEPT_FACE",FACE,{"disambiguationData":[OSD([sQuery(id+"F1.wireOp",EDGE,"E73.2.9"),sQuery(id+"F1.wireOp",EDGE,"E73.2.15")])]})]});
            var Q1;
            Q1=makeQuery(id+"F5.opChamfer","BLEND_EDGE",EDGE,{"blendedFrom":[makeQuery(id+"F3.opExtrude","CAP_EDGE",EDGE,{"disambiguationData":[OSD([sQuery(id+"F1.wireOp",EDGE,"E61"),sQuery(id+"F1.wireOp",EDGE,"E65.MirrorCS")])],"isStart":false}),makeQuery(id+"F3.opExtrude","SWEPT_FACE",FACE,{"disambiguationData":[OSD([sQuery(id+"F1.wireOp",EDGE,"E62"),sQuery(id+"F1.wireOp",EDGE,"E63.top")])]})],"blendedInto":[makeQuery(id+"F3.opExtrude","SWEPT_FACE",FACE,{"disambiguationData":[OSD([sQuery(id+"F1.wireOp",EDGE,"E62"),sQuery(id+"F1.wireOp",EDGE,"E63.top")])]})]});
            var Q2;
            Q2=makeQuery(id+"F5.opChamfer","BLEND_EDGE",EDGE,{"blendedFrom":[makeQuery(id+"F3.opExtrude","CAP_EDGE",EDGE,{"disambiguationData":[OSD([sQuery(id+"F1.wireOp",EDGE,"E61"),sQuery(id+"F1.wireOp",EDGE,"E65.MirrorCS")])],"isStart":false}),makeQuery(id+"F3.opExtrude","SWEPT_FACE",FACE,{"disambiguationData":[OSD([sQuery(id+"F1.wireOp",EDGE,"E62"),sQuery(id+"F1.wireOp",EDGE,"E67.MirrorCS")])]})],"blendedInto":[makeQuery(id+"F3.opExtrude","SWEPT_FACE",FACE,{"disambiguationData":[OSD([sQuery(id+"F1.wireOp",EDGE,"E62"),sQuery(id+"F1.wireOp",EDGE,"E67.MirrorCS")])]})]});
            var Q3;
            Q3=makeQuery(id+"F5.opChamfer","BLEND_EDGE",EDGE,{"blendedFrom":[makeQuery(id+"F3.opExtrude","CAP_EDGE",EDGE,{"disambiguationData":[OSD([sQuery(id+"F1.wireOp",EDGE,"E73.1.6"),sQuery(id+"F1.wireOp",EDGE,"E73.1.13")])],"isStart":false}),makeQuery(id+"F3.opExtrude","SWEPT_FACE",FACE,{"disambiguationData":[OSD([sQuery(id+"F1.wireOp",EDGE,"E73.1.9"),sQuery(id+"F1.wireOp",EDGE,"E73.1.12")])]})],"blendedInto":[makeQuery(id+"F3.opExtrude","SWEPT_FACE",FACE,{"disambiguationData":[OSD([sQuery(id+"F1.wireOp",EDGE,"E73.1.9"),sQuery(id+"F1.wireOp",EDGE,"E73.1.12")])]})]});
            var Q4;
            Q4=makeQuery(id+"F5.opChamfer","BLEND_EDGE",EDGE,{"blendedFrom":[makeQuery(id+"F3.opExtrude","CAP_EDGE",EDGE,{"disambiguationData":[OSD([sQuery(id+"F1.wireOp",EDGE,"E73.1.6"),sQuery(id+"F1.wireOp",EDGE,"E73.1.13")])],"isStart":false}),makeQuery(id+"F3.opExtrude","SWEPT_FACE",FACE,{"disambiguationData":[OSD([sQuery(id+"F1.wireOp",EDGE,"E73.1.9"),sQuery(id+"F1.wireOp",EDGE,"E73.1.15")])]})],"blendedInto":[makeQuery(id+"F3.opExtrude","SWEPT_FACE",FACE,{"disambiguationData":[OSD([sQuery(id+"F1.wireOp",EDGE,"E73.1.9"),sQuery(id+"F1.wireOp",EDGE,"E73.1.15")])]})]});
            var Q5;
            Q5=makeQuery(id+"F5.opChamfer","BLEND_EDGE",EDGE,{"blendedFrom":[makeQuery(id+"F3.opExtrude","CAP_EDGE",EDGE,{"disambiguationData":[OSD([sQuery(id+"F1.wireOp",EDGE,"E73.2.6"),sQuery(id+"F1.wireOp",EDGE,"E73.2.13")])],"isStart":false}),makeQuery(id+"F3.opExtrude","SWEPT_FACE",FACE,{"disambiguationData":[OSD([sQuery(id+"F1.wireOp",EDGE,"E73.2.9"),sQuery(id+"F1.wireOp",EDGE,"E73.2.12")])]})],"blendedInto":[makeQuery(id+"F3.opExtrude","SWEPT_FACE",FACE,{"disambiguationData":[OSD([sQuery(id+"F1.wireOp",EDGE,"E73.2.9"),sQuery(id+"F1.wireOp",EDGE,"E73.2.12")])]})]});
            var Q6;
            Q6=makeQuery(id+"F5.opChamfer","BLEND_EDGE",EDGE,{"blendedFrom":[makeQuery(id+"F3.opExtrude","CAP_EDGE",EDGE,{"disambiguationData":[OSD([sQuery(id+"F1.wireOp",EDGE,"E61"),sQuery(id+"F1.wireOp",EDGE,"E65.MirrorCS")])],"isStart":false}),makeQuery(id+"F3.opExtrude","SWEPT_FACE",FACE,{"disambiguationData":[OSD([sQuery(id+"F1.wireOp",EDGE,"E66.MirrorCS")])]})],"blendedInto":[makeQuery(id+"F3.opExtrude","SWEPT_FACE",FACE,{"disambiguationData":[OSD([sQuery(id+"F1.wireOp",EDGE,"E66.MirrorCS")])]})]});
            var Q7;
            Q7=makeQuery(id+"F5.opChamfer","BLEND_EDGE",EDGE,{"blendedFrom":[makeQuery(id+"F3.opExtrude","CAP_EDGE",EDGE,{"disambiguationData":[OSD([sQuery(id+"F1.wireOp",EDGE,"E61"),sQuery(id+"F1.wireOp",EDGE,"E65.MirrorCS")])],"isStart":false}),makeQuery(id+"F3.opExtrude","SWEPT_FACE",FACE,{"disambiguationData":[OSD([sQuery(id+"F1.wireOp",EDGE,"E63.right")])]})],"blendedInto":[makeQuery(id+"F3.opExtrude","SWEPT_FACE",FACE,{"disambiguationData":[OSD([sQuery(id+"F1.wireOp",EDGE,"E63.right")])]})]});
            var Q8;
            Q8=makeQuery(id+"F5.opChamfer","BLEND_EDGE",EDGE,{"blendedFrom":[makeQuery(id+"F3.opExtrude","CAP_EDGE",EDGE,{"disambiguationData":[OSD([sQuery(id+"F1.wireOp",EDGE,"E73.1.6"),sQuery(id+"F1.wireOp",EDGE,"E73.1.13")])],"isStart":false}),makeQuery(id+"F3.opExtrude","SWEPT_FACE",FACE,{"disambiguationData":[OSD([sQuery(id+"F1.wireOp",EDGE,"E73.1.0")])]})],"blendedInto":[makeQuery(id+"F3.opExtrude","SWEPT_FACE",FACE,{"disambiguationData":[OSD([sQuery(id+"F1.wireOp",EDGE,"E73.1.0")])]})]});
            var Q9;
            Q9=makeQuery(id+"F5.opChamfer","BLEND_EDGE",EDGE,{"blendedFrom":[makeQuery(id+"F3.opExtrude","CAP_EDGE",EDGE,{"disambiguationData":[OSD([sQuery(id+"F1.wireOp",EDGE,"E73.1.6"),sQuery(id+"F1.wireOp",EDGE,"E73.1.13")])],"isStart":false}),makeQuery(id+"F3.opExtrude","SWEPT_FACE",FACE,{"disambiguationData":[OSD([sQuery(id+"F1.wireOp",EDGE,"E73.1.5")])]})],"blendedInto":[makeQuery(id+"F3.opExtrude","SWEPT_FACE",FACE,{"disambiguationData":[OSD([sQuery(id+"F1.wireOp",EDGE,"E73.1.5")])]})]});
            var Q10;
            Q10=makeQuery(id+"F5.opChamfer","BLEND_EDGE",EDGE,{"blendedFrom":[makeQuery(id+"F3.opExtrude","CAP_EDGE",EDGE,{"disambiguationData":[OSD([sQuery(id+"F1.wireOp",EDGE,"E73.2.6"),sQuery(id+"F1.wireOp",EDGE,"E73.2.13")])],"isStart":false}),makeQuery(id+"F3.opExtrude","SWEPT_FACE",FACE,{"disambiguationData":[OSD([sQuery(id+"F1.wireOp",EDGE,"E73.2.5")])]})],"blendedInto":[makeQuery(id+"F3.opExtrude","SWEPT_FACE",FACE,{"disambiguationData":[OSD([sQuery(id+"F1.wireOp",EDGE,"E73.2.5")])]})]});
            var Q11;
            Q11=makeQuery(id+"F5.opChamfer","BLEND_EDGE",EDGE,{"blendedFrom":[makeQuery(id+"F3.opExtrude","CAP_EDGE",EDGE,{"disambiguationData":[OSD([sQuery(id+"F1.wireOp",EDGE,"E73.2.6"),sQuery(id+"F1.wireOp",EDGE,"E73.2.13")])],"isStart":false}),makeQuery(id+"F3.opExtrude","SWEPT_FACE",FACE,{"disambiguationData":[OSD([sQuery(id+"F1.wireOp",EDGE,"E73.2.0")])]})],"blendedInto":[makeQuery(id+"F3.opExtrude","SWEPT_FACE",FACE,{"disambiguationData":[OSD([sQuery(id+"F1.wireOp",EDGE,"E73.2.0")])]})]});
            var Q12;
            Q12=makeQuery(id+"F5.opChamfer","BLEND_EDGE",EDGE,{"blendedFrom":[makeQuery(id+"F3.opExtrude","CAP_EDGE",EDGE,{"disambiguationData":[OSD([sQuery(id+"F1.wireOp",EDGE,"E73.2.6"),sQuery(id+"F1.wireOp",EDGE,"E73.2.13")])],"isStart":false}),makeQuery(id+"F3.opExtrude","SWEPT_FACE",FACE,{"disambiguationData":[OSD([sQuery(id+"F1.wireOp",EDGE,"E73.2.1")])]})],"blendedInto":[makeQuery(id+"F3.opExtrude","SWEPT_FACE",FACE,{"disambiguationData":[OSD([sQuery(id+"F1.wireOp",EDGE,"E73.2.1")])]})]});
            var Q13;
            {var subQ0=sQuery(id+"F1.wireOp",EDGE,"E73.2.6");Q13=makeQuery(id+"F5.opChamfer","BLEND_EDGE",EDGE,{"blendedFrom":[makeQuery(id+"F3.opExtrude","CAP_EDGE",EDGE,{"disambiguationData":[OSD([subQ0,sQuery(id+"F1.wireOp",EDGE,"E73.2.13")])],"isStart":false}),makeQuery(id+"F2.opExtrude","CAP_FACE",FACE,{"disambiguationData":[OSD([sQuery(id+"F1.wireOp",EDGE,"E61"),sQuery(id+"F1.wireOp",EDGE,"E62"),sQuery(id+"F1.wireOp",EDGE,"f1ae98ec-eddd-4e72-9429-8ecdf1ed458a"),sQuery(id+"F1.wireOp",EDGE,"4aa6aff6-2e9c-42ca-a4fd-632af8ab0357"),sQuery(id+"F1.wireOp",EDGE,"E63.top"),sQuery(id+"F1.wireOp",EDGE,"E67.MirrorCS"),sQuery(id+"F1.wireOp",EDGE,"E69.MirrorCS"),sQuery(id+"F1.wireOp",EDGE,"E71.MirrorCS"),sQuery(id+"F1.wireOp",EDGE,"E73.1.1"),sQuery(id+"F1.wireOp",EDGE,"E73.1.2"),sQuery(id+"F1.wireOp",EDGE,"E73.1.6"),sQuery(id+"F1.wireOp",EDGE,"E73.1.9"),sQuery(id+"F1.wireOp",EDGE,"E73.1.10"),sQuery(id+"F1.wireOp",EDGE,"E73.1.11"),sQuery(id+"F1.wireOp",EDGE,"E73.1.12"),sQuery(id+"F1.wireOp",EDGE,"E73.1.15"),sQuery(id+"F1.wireOp",EDGE,"E73.2.1"),sQuery(id+"F1.wireOp",EDGE,"E73.2.2"),subQ0,sQuery(id+"F1.wireOp",EDGE,"E73.2.9"),sQuery(id+"F1.wireOp",EDGE,"E73.2.10"),sQuery(id+"F1.wireOp",EDGE,"E73.2.11"),sQuery(id+"F1.wireOp",EDGE,"E73.2.12"),sQuery(id+"F1.wireOp",EDGE,"E73.2.15"),sQuery(id+"F1.wireOp",EDGE,"E74"),sQuery(id+"F1.wireOp",EDGE,"E75"),sQuery(id+"F1.wireOp",EDGE,"E76")])],"isStart":false})],"blendedInto":[makeQuery(id+"F2.opExtrude","CAP_FACE",FACE,{"disambiguationData":[OSD([sQuery(id+"F1.wireOp",EDGE,"E61"),sQuery(id+"F1.wireOp",EDGE,"E62"),sQuery(id+"F1.wireOp",EDGE,"f1ae98ec-eddd-4e72-9429-8ecdf1ed458a"),sQuery(id+"F1.wireOp",EDGE,"4aa6aff6-2e9c-42ca-a4fd-632af8ab0357"),sQuery(id+"F1.wireOp",EDGE,"E63.top"),sQuery(id+"F1.wireOp",EDGE,"E67.MirrorCS"),sQuery(id+"F1.wireOp",EDGE,"E69.MirrorCS"),sQuery(id+"F1.wireOp",EDGE,"E71.MirrorCS"),sQuery(id+"F1.wireOp",EDGE,"E73.1.1"),sQuery(id+"F1.wireOp",EDGE,"E73.1.2"),sQuery(id+"F1.wireOp",EDGE,"E73.1.6"),sQuery(id+"F1.wireOp",EDGE,"E73.1.9"),sQuery(id+"F1.wireOp",EDGE,"E73.1.10"),sQuery(id+"F1.wireOp",EDGE,"E73.1.11"),sQuery(id+"F1.wireOp",EDGE,"E73.1.12"),sQuery(id+"F1.wireOp",EDGE,"E73.1.15"),sQuery(id+"F1.wireOp",EDGE,"E73.2.1"),sQuery(id+"F1.wireOp",EDGE,"E73.2.2"),subQ0,sQuery(id+"F1.wireOp",EDGE,"E73.2.9"),sQuery(id+"F1.wireOp",EDGE,"E73.2.10"),sQuery(id+"F1.wireOp",EDGE,"E73.2.11"),sQuery(id+"F1.wireOp",EDGE,"E73.2.12"),sQuery(id+"F1.wireOp",EDGE,"E73.2.15"),sQuery(id+"F1.wireOp",EDGE,"E74"),sQuery(id+"F1.wireOp",EDGE,"E75"),sQuery(id+"F1.wireOp",EDGE,"E76")])],"isStart":false})]});}
            var Q14;
            Q14=makeQuery(id+"F5.opChamfer","BLEND_EDGE",EDGE,{"blendedFrom":[makeQuery(id+"F3.opExtrude","CAP_EDGE",EDGE,{"disambiguationData":[OSD([sQuery(id+"F1.wireOp",EDGE,"E73.2.6"),sQuery(id+"F1.wireOp",EDGE,"E73.2.13")])],"isStart":false}),makeQuery(id+"F3.opExtrude","SWEPT_FACE",FACE,{"disambiguationData":[OSD([sQuery(id+"F1.wireOp",EDGE,"E73.2.2")])]})],"blendedInto":[makeQuery(id+"F3.opExtrude","SWEPT_FACE",FACE,{"disambiguationData":[OSD([sQuery(id+"F1.wireOp",EDGE,"E73.2.2")])]})]});
            var Q15;
            Q15=makeQuery(id+"F5.opChamfer","BLEND_EDGE",EDGE,{"blendedFrom":[makeQuery(id+"F3.opExtrude","CAP_EDGE",EDGE,{"disambiguationData":[OSD([sQuery(id+"F1.wireOp",EDGE,"E73.1.6"),sQuery(id+"F1.wireOp",EDGE,"E73.1.13")])],"isStart":false}),makeQuery(id+"F3.opExtrude","SWEPT_FACE",FACE,{"disambiguationData":[OSD([sQuery(id+"F1.wireOp",EDGE,"E73.1.2")])]})],"blendedInto":[makeQuery(id+"F3.opExtrude","SWEPT_FACE",FACE,{"disambiguationData":[OSD([sQuery(id+"F1.wireOp",EDGE,"E73.1.2")])]})]});
            var Q16;
            {var subQ0=sQuery(id+"F1.wireOp",EDGE,"E73.1.6");Q16=makeQuery(id+"F5.opChamfer","BLEND_EDGE",EDGE,{"blendedFrom":[makeQuery(id+"F3.opExtrude","CAP_EDGE",EDGE,{"disambiguationData":[OSD([subQ0,sQuery(id+"F1.wireOp",EDGE,"E73.1.13")])],"isStart":false}),makeQuery(id+"F2.opExtrude","CAP_FACE",FACE,{"disambiguationData":[OSD([sQuery(id+"F1.wireOp",EDGE,"E61"),sQuery(id+"F1.wireOp",EDGE,"E62"),sQuery(id+"F1.wireOp",EDGE,"f1ae98ec-eddd-4e72-9429-8ecdf1ed458a"),sQuery(id+"F1.wireOp",EDGE,"4aa6aff6-2e9c-42ca-a4fd-632af8ab0357"),sQuery(id+"F1.wireOp",EDGE,"E63.top"),sQuery(id+"F1.wireOp",EDGE,"E67.MirrorCS"),sQuery(id+"F1.wireOp",EDGE,"E69.MirrorCS"),sQuery(id+"F1.wireOp",EDGE,"E71.MirrorCS"),sQuery(id+"F1.wireOp",EDGE,"E73.1.1"),sQuery(id+"F1.wireOp",EDGE,"E73.1.2"),subQ0,sQuery(id+"F1.wireOp",EDGE,"E73.1.9"),sQuery(id+"F1.wireOp",EDGE,"E73.1.10"),sQuery(id+"F1.wireOp",EDGE,"E73.1.11"),sQuery(id+"F1.wireOp",EDGE,"E73.1.12"),sQuery(id+"F1.wireOp",EDGE,"E73.1.15"),sQuery(id+"F1.wireOp",EDGE,"E73.2.1"),sQuery(id+"F1.wireOp",EDGE,"E73.2.2"),sQuery(id+"F1.wireOp",EDGE,"E73.2.6"),sQuery(id+"F1.wireOp",EDGE,"E73.2.9"),sQuery(id+"F1.wireOp",EDGE,"E73.2.10"),sQuery(id+"F1.wireOp",EDGE,"E73.2.11"),sQuery(id+"F1.wireOp",EDGE,"E73.2.12"),sQuery(id+"F1.wireOp",EDGE,"E73.2.15"),sQuery(id+"F1.wireOp",EDGE,"E74"),sQuery(id+"F1.wireOp",EDGE,"E75"),sQuery(id+"F1.wireOp",EDGE,"E76")])],"isStart":false})],"blendedInto":[makeQuery(id+"F2.opExtrude","CAP_FACE",FACE,{"disambiguationData":[OSD([sQuery(id+"F1.wireOp",EDGE,"E61"),sQuery(id+"F1.wireOp",EDGE,"E62"),sQuery(id+"F1.wireOp",EDGE,"f1ae98ec-eddd-4e72-9429-8ecdf1ed458a"),sQuery(id+"F1.wireOp",EDGE,"4aa6aff6-2e9c-42ca-a4fd-632af8ab0357"),sQuery(id+"F1.wireOp",EDGE,"E63.top"),sQuery(id+"F1.wireOp",EDGE,"E67.MirrorCS"),sQuery(id+"F1.wireOp",EDGE,"E69.MirrorCS"),sQuery(id+"F1.wireOp",EDGE,"E71.MirrorCS"),sQuery(id+"F1.wireOp",EDGE,"E73.1.1"),sQuery(id+"F1.wireOp",EDGE,"E73.1.2"),subQ0,sQuery(id+"F1.wireOp",EDGE,"E73.1.9"),sQuery(id+"F1.wireOp",EDGE,"E73.1.10"),sQuery(id+"F1.wireOp",EDGE,"E73.1.11"),sQuery(id+"F1.wireOp",EDGE,"E73.1.12"),sQuery(id+"F1.wireOp",EDGE,"E73.1.15"),sQuery(id+"F1.wireOp",EDGE,"E73.2.1"),sQuery(id+"F1.wireOp",EDGE,"E73.2.2"),sQuery(id+"F1.wireOp",EDGE,"E73.2.6"),sQuery(id+"F1.wireOp",EDGE,"E73.2.9"),sQuery(id+"F1.wireOp",EDGE,"E73.2.10"),sQuery(id+"F1.wireOp",EDGE,"E73.2.11"),sQuery(id+"F1.wireOp",EDGE,"E73.2.12"),sQuery(id+"F1.wireOp",EDGE,"E73.2.15"),sQuery(id+"F1.wireOp",EDGE,"E74"),sQuery(id+"F1.wireOp",EDGE,"E75"),sQuery(id+"F1.wireOp",EDGE,"E76")])],"isStart":false})]});}
            var Q17;
            Q17=makeQuery(id+"F5.opChamfer","BLEND_EDGE",EDGE,{"blendedFrom":[makeQuery(id+"F3.opExtrude","CAP_EDGE",EDGE,{"disambiguationData":[OSD([sQuery(id+"F1.wireOp",EDGE,"E73.1.6"),sQuery(id+"F1.wireOp",EDGE,"E73.1.13")])],"isStart":false}),makeQuery(id+"F3.opExtrude","SWEPT_FACE",FACE,{"disambiguationData":[OSD([sQuery(id+"F1.wireOp",EDGE,"E73.1.1")])]})],"blendedInto":[makeQuery(id+"F3.opExtrude","SWEPT_FACE",FACE,{"disambiguationData":[OSD([sQuery(id+"F1.wireOp",EDGE,"E73.1.1")])]})]});
            var Q18;
            Q18=makeQuery(id+"F5.opChamfer","BLEND_EDGE",EDGE,{"blendedFrom":[makeQuery(id+"F3.opExtrude","CAP_EDGE",EDGE,{"disambiguationData":[OSD([sQuery(id+"F1.wireOp",EDGE,"E61"),sQuery(id+"F1.wireOp",EDGE,"E65.MirrorCS")])],"isStart":false}),makeQuery(id+"F3.opExtrude","SWEPT_FACE",FACE,{"disambiguationData":[OSD([sQuery(id+"F1.wireOp",EDGE,"E71.MirrorCS")])]})],"blendedInto":[makeQuery(id+"F3.opExtrude","SWEPT_FACE",FACE,{"disambiguationData":[OSD([sQuery(id+"F1.wireOp",EDGE,"E71.MirrorCS")])]})]});
            var Q19;
            {var subQ0=sQuery(id+"F1.wireOp",EDGE,"E61");Q19=makeQuery(id+"F5.opChamfer","BLEND_EDGE",EDGE,{"blendedFrom":[makeQuery(id+"F3.opExtrude","CAP_EDGE",EDGE,{"disambiguationData":[OSD([subQ0,sQuery(id+"F1.wireOp",EDGE,"E65.MirrorCS")])],"isStart":false}),makeQuery(id+"F2.opExtrude","CAP_FACE",FACE,{"disambiguationData":[OSD([subQ0,sQuery(id+"F1.wireOp",EDGE,"E62"),sQuery(id+"F1.wireOp",EDGE,"f1ae98ec-eddd-4e72-9429-8ecdf1ed458a"),sQuery(id+"F1.wireOp",EDGE,"4aa6aff6-2e9c-42ca-a4fd-632af8ab0357"),sQuery(id+"F1.wireOp",EDGE,"E63.top"),sQuery(id+"F1.wireOp",EDGE,"E67.MirrorCS"),sQuery(id+"F1.wireOp",EDGE,"E69.MirrorCS"),sQuery(id+"F1.wireOp",EDGE,"E71.MirrorCS"),sQuery(id+"F1.wireOp",EDGE,"E73.1.1"),sQuery(id+"F1.wireOp",EDGE,"E73.1.2"),sQuery(id+"F1.wireOp",EDGE,"E73.1.6"),sQuery(id+"F1.wireOp",EDGE,"E73.1.9"),sQuery(id+"F1.wireOp",EDGE,"E73.1.10"),sQuery(id+"F1.wireOp",EDGE,"E73.1.11"),sQuery(id+"F1.wireOp",EDGE,"E73.1.12"),sQuery(id+"F1.wireOp",EDGE,"E73.1.15"),sQuery(id+"F1.wireOp",EDGE,"E73.2.1"),sQuery(id+"F1.wireOp",EDGE,"E73.2.2"),sQuery(id+"F1.wireOp",EDGE,"E73.2.6"),sQuery(id+"F1.wireOp",EDGE,"E73.2.9"),sQuery(id+"F1.wireOp",EDGE,"E73.2.10"),sQuery(id+"F1.wireOp",EDGE,"E73.2.11"),sQuery(id+"F1.wireOp",EDGE,"E73.2.12"),sQuery(id+"F1.wireOp",EDGE,"E73.2.15"),sQuery(id+"F1.wireOp",EDGE,"E74"),sQuery(id+"F1.wireOp",EDGE,"E75"),sQuery(id+"F1.wireOp",EDGE,"E76")])],"isStart":false})],"blendedInto":[makeQuery(id+"F2.opExtrude","CAP_FACE",FACE,{"disambiguationData":[OSD([subQ0,sQuery(id+"F1.wireOp",EDGE,"E62"),sQuery(id+"F1.wireOp",EDGE,"f1ae98ec-eddd-4e72-9429-8ecdf1ed458a"),sQuery(id+"F1.wireOp",EDGE,"4aa6aff6-2e9c-42ca-a4fd-632af8ab0357"),sQuery(id+"F1.wireOp",EDGE,"E63.top"),sQuery(id+"F1.wireOp",EDGE,"E67.MirrorCS"),sQuery(id+"F1.wireOp",EDGE,"E69.MirrorCS"),sQuery(id+"F1.wireOp",EDGE,"E71.MirrorCS"),sQuery(id+"F1.wireOp",EDGE,"E73.1.1"),sQuery(id+"F1.wireOp",EDGE,"E73.1.2"),sQuery(id+"F1.wireOp",EDGE,"E73.1.6"),sQuery(id+"F1.wireOp",EDGE,"E73.1.9"),sQuery(id+"F1.wireOp",EDGE,"E73.1.10"),sQuery(id+"F1.wireOp",EDGE,"E73.1.11"),sQuery(id+"F1.wireOp",EDGE,"E73.1.12"),sQuery(id+"F1.wireOp",EDGE,"E73.1.15"),sQuery(id+"F1.wireOp",EDGE,"E73.2.1"),sQuery(id+"F1.wireOp",EDGE,"E73.2.2"),sQuery(id+"F1.wireOp",EDGE,"E73.2.6"),sQuery(id+"F1.wireOp",EDGE,"E73.2.9"),sQuery(id+"F1.wireOp",EDGE,"E73.2.10"),sQuery(id+"F1.wireOp",EDGE,"E73.2.11"),sQuery(id+"F1.wireOp",EDGE,"E73.2.12"),sQuery(id+"F1.wireOp",EDGE,"E73.2.15"),sQuery(id+"F1.wireOp",EDGE,"E74"),sQuery(id+"F1.wireOp",EDGE,"E75"),sQuery(id+"F1.wireOp",EDGE,"E76")])],"isStart":false})]});}
            var Q20;
            Q20=makeQuery(id+"F5.opChamfer","BLEND_EDGE",EDGE,{"blendedFrom":[makeQuery(id+"F3.opExtrude","CAP_EDGE",EDGE,{"disambiguationData":[OSD([sQuery(id+"F1.wireOp",EDGE,"E61"),sQuery(id+"F1.wireOp",EDGE,"E65.MirrorCS")])],"isStart":false}),makeQuery(id+"F3.opExtrude","SWEPT_FACE",FACE,{"disambiguationData":[OSD([sQuery(id+"F1.wireOp",EDGE,"E69.MirrorCS")])]})],"blendedInto":[makeQuery(id+"F3.opExtrude","SWEPT_FACE",FACE,{"disambiguationData":[OSD([sQuery(id+"F1.wireOp",EDGE,"E69.MirrorCS")])]})]});
            var Q21;
            Q21=makeQuery(id+"F2.opExtrude","CAP_EDGE",EDGE,{"disambiguationData":[OSD([sQuery(id+"F1.wireOp",EDGE,"E73.1.9"),sQuery(id+"F1.wireOp",EDGE,"E73.1.12")])],"isStart":false});
            var Q22;
            Q22=makeQuery(id+"F2.opExtrude","CAP_EDGE",EDGE,{"disambiguationData":[OSD([sQuery(id+"F1.wireOp",EDGE,"E62"),sQuery(id+"F1.wireOp",EDGE,"E67.MirrorCS")])],"isStart":false});
            var Q23;
            Q23=makeQuery(id+"F2.opExtrude","CAP_EDGE",EDGE,{"disambiguationData":[OSD([sQuery(id+"F1.wireOp",EDGE,"E71.MirrorCS")])],"isStart":false});
            var Q24;
            Q24=makeQuery(id+"F2.opExtrude","CAP_EDGE",EDGE,{"disambiguationData":[OSD([sQuery(id+"F1.wireOp",EDGE,"E62"),sQuery(id+"F1.wireOp",EDGE,"E63.top")])],"isStart":false});
            var Q25;
            Q25=makeQuery(id+"F2.opExtrude","CAP_EDGE",EDGE,{"disambiguationData":[OSD([sQuery(id+"F1.wireOp",EDGE,"E69.MirrorCS")])],"isStart":false});
            var Q26;
            Q26=makeQuery(id+"F2.opExtrude","CAP_EDGE",EDGE,{"disambiguationData":[OSD([sQuery(id+"F1.wireOp",EDGE,"E73.2.2")])],"isStart":false});
            var Q27;
            Q27=makeQuery(id+"F2.opExtrude","CAP_EDGE",EDGE,{"disambiguationData":[OSD([sQuery(id+"F1.wireOp",EDGE,"E73.1.9"),sQuery(id+"F1.wireOp",EDGE,"E73.1.15")])],"isStart":false});
            var Q28;
            Q28=makeQuery(id+"F2.opExtrude","CAP_EDGE",EDGE,{"disambiguationData":[OSD([sQuery(id+"F1.wireOp",EDGE,"E73.1.2")])],"isStart":false});
            var Q29;
            Q29=makeQuery(id+"F2.opExtrude","CAP_EDGE",EDGE,{"disambiguationData":[OSD([sQuery(id+"F1.wireOp",EDGE,"E73.2.9"),sQuery(id+"F1.wireOp",EDGE,"E73.2.12")])],"isStart":false});
            var Q30;
            Q30=makeQuery(id+"F2.opExtrude","CAP_EDGE",EDGE,{"disambiguationData":[OSD([sQuery(id+"F1.wireOp",EDGE,"E73.2.1")])],"isStart":false});
            var Q31;
            Q31=makeQuery(id+"F2.opExtrude","CAP_EDGE",EDGE,{"disambiguationData":[OSD([sQuery(id+"F1.wireOp",EDGE,"E73.1.1")])],"isStart":false});
            fillet(context, id + "F13", {"entities" : qUnion([Q0, Q1, Q2, Q3, Q4, Q5, Q6, Q7, Q8, Q9, Q10, Q11, Q12, Q13, Q14, Q15, Q16, Q17, Q18, Q19, Q20, Q21, Q22, Q23, Q24, Q25, Q26, Q27, Q28, Q29, Q30, Q31]), "radius" : 1.5 * mm, "tangentPropagation" : true, "allowEdgeOverflow" : false});
        }
        {
            var Q0;
            Q0=makeQuery(id+"F10.imprint","IMPRINT",FACE,{"disambiguationData":[TD([[makeQuery(id+"F10.imprint","IMPRINT",EDGE,{"derivedFrom":sQuery(id+"F10.wireOp",EDGE,"E117")}),1.0]])]});
            var Q1;
            Q1=makeQuery(id+"F10.imprint","IMPRINT",FACE,{"disambiguationData":[TD([[makeQuery(id+"F10.imprint","IMPRINT",EDGE,{"derivedFrom":sQuery(id+"F10.wireOp",EDGE,"E118")}),1.0]])]});
            extrude(context, id + "F14", {"entities" : qUnion([Q0, Q1]), "operationType" : NewBodyOperationType.REMOVE, "oppositeDirection" : true, "depth" : 4 * mm});
        }
        {
            var Q0;
            Q0=makeQuery(id+"F9.imprint","IMPRINT",FACE,{"disambiguationData":[TD([[makeQuery(id+"F9.imprint","IMPRINT",EDGE,{"derivedFrom":sQuery(id+"F9.wireOp",EDGE,"E111")}),1.0]])]});
            var Q1;
            Q1=makeQuery(id+"F9.imprint","IMPRINT",FACE,{"disambiguationData":[TD([[makeQuery(id+"F9.imprint","IMPRINT",EDGE,{"derivedFrom":sQuery(id+"F9.wireOp",EDGE,"E110")}),1.0]])]});
            extrude(context, id + "F15", {"entities" : qUnion([Q0, Q1]), "operationType" : NewBodyOperationType.REMOVE, "oppositeDirection" : true, "depth" : 4 * mm});
        }
        {
            var Q0;
            Q0=makeQuery(id+"F8.imprint","IMPRINT",FACE,{"disambiguationData":[TD([[makeQuery(id+"F8.imprint","IMPRINT",EDGE,{"derivedFrom":sQuery(id+"F8.wireOp",EDGE,"E106")}),1.0]])]});
            var Q1;
            Q1=makeQuery(id+"F7.imprint","IMPRINT",FACE,{"disambiguationData":[TD([[makeQuery(id+"F7.imprint","IMPRINT",EDGE,{"derivedFrom":sQuery(id+"F7.wireOp",EDGE,"E104")}),1.0]])]});
            var Q2;
            Q2=makeQuery(id+"F11.boolean.opBoolean","SPLIT",FACE,{"disambiguationData":[TD([makeQuery(id+"F11.opExtrude","SWEPT_FACE",FACE,{"disambiguationData":[OSD([sQuery(id+"F6.wireOp",EDGE,"E100")])]})])],"derivedFrom":makeQuery(id+"F5.opChamfer","BLEND_FACE",FACE,{"disambiguationData":[OSD([sQuery(id+"F0.wireOp",EDGE,"E10"),sQuery(id+"F0.wireOp",EDGE,"E50.bottom")])]})});
            var Q3;
            Q3=makeQuery(id+"F11.boolean.opBoolean","SPLIT",FACE,{"disambiguationData":[TD([makeQuery(id+"F11.opExtrude","SWEPT_FACE",FACE,{"disambiguationData":[OSD([sQuery(id+"F6.wireOp",EDGE,"E101")])]})])],"derivedFrom":makeQuery(id+"F5.opChamfer","BLEND_FACE",FACE,{"disambiguationData":[OSD([sQuery(id+"F0.wireOp",EDGE,"E10"),sQuery(id+"F0.wireOp",EDGE,"E50.bottom")])]})});
            extrude(context, id + "F16", {"entities" : qUnion([Q0, Q1, Q2, Q3]), "operationType" : NewBodyOperationType.REMOVE, "oppositeDirection" : true, "depth" : 8 * mm});
        }
        {
            var Q0;
            Q0=makeQuery(id+"F14.boolean.opBoolean","SPLIT",FACE,{"disambiguationData":[TD([makeQuery(id+"F14.opExtrude","SWEPT_FACE",FACE,{"disambiguationData":[OSD([sQuery(id+"F10.wireOp",EDGE,"E120")])]})])],"derivedFrom":makeQuery(id+"F5.opChamfer","BLEND_FACE",FACE,{"disambiguationData":[OSD([sQuery(id+"F1.wireOp",EDGE,"E73.2.6"),sQuery(id+"F1.wireOp",EDGE,"E73.2.13")])]})});
            var Q1;
            Q1=makeQuery(id+"F14.boolean.opBoolean","SPLIT",FACE,{"disambiguationData":[TD([makeQuery(id+"F14.opExtrude","SWEPT_FACE",FACE,{"disambiguationData":[OSD([sQuery(id+"F10.wireOp",EDGE,"E119")])]})])],"derivedFrom":makeQuery(id+"F5.opChamfer","BLEND_FACE",FACE,{"disambiguationData":[OSD([sQuery(id+"F1.wireOp",EDGE,"E73.2.6"),sQuery(id+"F1.wireOp",EDGE,"E73.2.13")])]})});
            extrude(context, id + "F17", {"entities" : qUnion([Q0, Q1]), "operationType" : NewBodyOperationType.REMOVE, "oppositeDirection" : true, "depth" : 8 * mm});
        }
        {
            var Q0;
            Q0=makeQuery(id+"F9.imprint","IMPRINT",FACE,{"disambiguationData":[TD([[makeQuery(id+"F9.imprint","IMPRINT",EDGE,{"derivedFrom":sQuery(id+"F9.wireOp",EDGE,"E113")}),1.0]])]});
            var Q1;
            Q1=makeQuery(id+"F9.imprint","IMPRINT",FACE,{"disambiguationData":[TD([[makeQuery(id+"F9.imprint","IMPRINT",EDGE,{"derivedFrom":sQuery(id+"F9.wireOp",EDGE,"E112")}),1.0]])]});
            extrude(context, id + "F18", {"entities" : qUnion([Q0, Q1]), "operationType" : NewBodyOperationType.REMOVE, "oppositeDirection" : true, "depth" : 8 * mm});
        }
        {
            var Q0;
            Q0=qCreatedBy(makeId("Top.planeOp"),FACE);
            var sketch = newSketch(context, id + "F19", { "sketchPlane" : qUnion([Q0])});
            skCircle(sketch, "E121", {"center": v(-81.36, -54.16) * mm, "radius": 3.5 * mm});
            skCircle(sketch, "E122", {"center": v(-81.36, -54.16) * mm, "radius": 1.75 * mm});
            skSolve(sketch);
        }
        {
            var Q0;
            Q0=makeQuery(id+"F19.imprint","IMPRINT",FACE,{"disambiguationData":[TD([[makeQuery(id+"F19.imprint","IMPRINT",EDGE,{"derivedFrom":sQuery(id+"F19.wireOp",EDGE,"E121")}),1.0]])]});
            extrude(context, id + "F20", {"entities" : qUnion([Q0]), "depth" : 20 * mm});
        }
        {
            var Q0;
            Q0=qCreatedBy(makeId("Top.planeOp"),FACE);
            var sketch = newSketch(context, id + "F21", { "sketchPlane" : qUnion([Q0])});
            skLineSegment(sketch, "E123.bottom", {"start": v(-122.76, -73.77) * mm, "end": v(-116.76, -73.77) * mm});
            skLineSegment(sketch, "E123.top", {"start": v(-122.76, -60.87) * mm, "end": v(-116.76, -60.87) * mm});
            skLineSegment(sketch, "E123.left", {"start": v(-122.76, -73.77) * mm, "end": v(-122.76, -60.87) * mm});
            skLineSegment(sketch, "E123.right", {"start": v(-116.76, -73.77) * mm, "end": v(-116.76, -60.87) * mm});
            skLineSegment(sketch, "E124.0", {"start": v(-124.76, -58.87) * mm, "end": v(-114.76, -58.87) * mm});
            skLineSegment(sketch, "E124.2", {"start": v(-124.76, -75.77) * mm, "end": v(-114.76, -75.77) * mm});
            skLineSegment(sketch, "E124.3", {"start": v(-114.76, -75.77) * mm, "end": v(-114.76, -58.87) * mm});
            skLineSegment(sketch, "E125.bottom", {"start": v(-124.76, -75.77) * mm, "end": v(-127.76, -75.77) * mm});
            skLineSegment(sketch, "E125.top", {"start": v(-124.76, -58.87) * mm, "end": v(-127.76, -58.87) * mm});
            skLineSegment(sketch, "E125.right", {"start": v(-127.76, -75.77) * mm, "end": v(-127.76, -58.87) * mm});
            skLineSegment(sketch, "E126", {"start": v(-122.76, -73.77) * mm, "end": v(-122.76, -75.77) * mm});
            skLineSegment(sketch, "E127", {"start": v(-122.76, -60.87) * mm, "end": v(-122.76, -58.87) * mm});
            skSolve(sketch);
        }
        {
            var Q0;
            Q0=makeQuery(id+"F21.imprint","IMPRINT",FACE,{"disambiguationData":[TD([[makeQuery(id+"F21.imprint","IMPRINT",EDGE,{"derivedFrom":sQuery(id+"F21.wireOp",EDGE,"E123.left")}),1.0]])]});
            extrude(context, id + "F22", {"entities" : qUnion([Q0]), "depth" : 30 * mm});
        }
        {
            var Q0;
            Q0=makeQuery(id+"F21.imprint","IMPRINT",FACE,{"disambiguationData":[TD([[makeQuery(id+"F21.imprint","IMPRINT",EDGE,{"derivedFrom":sQuery(id+"F21.wireOp",EDGE,"E123.bottom")}),-1.0]])]});
            extrude(context, id + "F23", {"entities" : qUnion([Q0]), "operationType" : NewBodyOperationType.ADD, "depth" : 7 * mm});
        }
        {
            var Q0;
            Q0=makeQuery(id+"F22.opExtrude","SWEPT_FACE",FACE,{"disambiguationData":[OSD([sQuery(id+"F21.wireOp",EDGE,"E123.left"),sQuery(id+"F21.wireOp",EDGE,"E126"),sQuery(id+"F21.wireOp",EDGE,"E127")])]});
            var sketch = newSketch(context, id + "F24", { "sketchPlane" : qUnion([Q0])});
            skLineSegment(sketch, "E128", {"start": v(-67.32, 30) * mm, "end": v(-67.32, 7) * mm, "construction": true});
            skCircle(sketch, "E129", {"center": v(-67.32, 24) * mm, "radius": 2 * mm});
            skCircle(sketch, "E130", {"center": v(-67.32, 11.94) * mm, "radius": 2 * mm});
            skSolve(sketch);
        }
        {
            var Q0;
            Q0=makeQuery(id+"F24.imprint","IMPRINT",FACE,{"disambiguationData":[TD([[makeQuery(id+"F24.imprint","IMPRINT",EDGE,{"derivedFrom":sQuery(id+"F24.wireOp",EDGE,"E129")}),1.0]])]});
            var Q1;
            Q1=makeQuery(id+"F24.imprint","IMPRINT",FACE,{"disambiguationData":[TD([[makeQuery(id+"F24.imprint","IMPRINT",EDGE,{"derivedFrom":sQuery(id+"F24.wireOp",EDGE,"E130")}),1.0]])]});
            extrude(context, id + "F25", {"entities" : qUnion([Q0, Q1]), "operationType" : NewBodyOperationType.REMOVE, "oppositeDirection" : true, "depth" : 25 * mm});
        }
        {
            var Q0;
            Q0=makeQuery(id+"F22.opExtrude","CAP_EDGE",EDGE,{"disambiguationData":[OSD([sQuery(id+"F21.wireOp",EDGE,"E124.2"),sQuery(id+"F21.wireOp",EDGE,"E125.bottom")])],"isStart":false});
            var Q1;
            Q1=makeQuery(id+"F22.opExtrude","CAP_EDGE",EDGE,{"disambiguationData":[OSD([sQuery(id+"F21.wireOp",EDGE,"E124.0"),sQuery(id+"F21.wireOp",EDGE,"E125.top")])],"isStart":false});
            var Q2;
            Q2=makeQuery(id+"F22.opExtrude","SWEPT_EDGE",EDGE,{"disambiguationData":[OSD([sQuery(id+"F21.wireOp",EDGE,"E124.2"),sQuery(id+"F21.wireOp",EDGE,"E126")])]});
            var Q3;
            Q3=makeQuery(id+"F22.opExtrude","SWEPT_EDGE",EDGE,{"disambiguationData":[OSD([sQuery(id+"F21.wireOp",EDGE,"E124.0"),sQuery(id+"F21.wireOp",EDGE,"E127")])]});
            fillet(context, id + "F26", {"entities" : qUnion([Q0, Q1, Q2, Q3]), "radius" : 5 * mm, "tangentPropagation" : true, "allowEdgeOverflow" : false});
        }
    });
